FREECAD ASSEMBLY — COMPONENT RECIPES ("roommake")

This assembly document has 24 components, labeled P0..P23 below (a component is one placed body or linked part). 22 of them carry a construction recipe — the FreeCAD feature program that regenerates the part from scratch, quoted from this document or its linked companion documents; the rest are supplied as boundary geometry only. No exploded tour is included for this assembly.
NOTE — document 2 of 3 of this assembly tour. The two overview renders and the header above are repeated from document 1; the component sections below continue where the previous document stopped.
COMPONENT P14 — recipe-attached ("sofa", a linked part whose construction recipe lives in a companion FreeCAD document of the same project; that document's serialized recipe follows).
Construction recipe (the companion document, serialized — sketch geometry with constraints, then the solid features built on it; lengths are millimeters unless a unit is written):

FCSTD DOCUMENT  (FreeCAD 1.0R39109 (Git))
Label: sofa
License: All rights reserved
LicenseURL: https://en.wikipedia.org/wiki/All_rights_reserved
objects: Sketcher::SketchObject×17, PartDesign::Pad×14, PartDesign::Fillet×11, PartDesign::Plane×9, PartDesign::Body×9, PartDesign::ShapeBinder×8, PartDesign::Pocket×3, App::Part×3, Part::FeaturePython×2, PartDesign::LinearPattern×1
note: 148 computed .brp shape members not serialized (recipe doc carries the construction recipe); baked Part::Feature solids carry a one-line shape summary decoded from their .brp

FEATURE [Sketcher::SketchObject] Sketch
  ArcFitTolerance = 1e-06
  AttachmentSupport = -> [XZ_Plane]
  FullyConstrained = true
  MakeInternals = false
  MapMode = 5
  Placement = pos=(0,0,0) rot=(1,0,0;1.5708rad)
  sketch-geometry (4):
    g0: LineSegment StartX=-300 StartY=380 StartZ=0 EndX=-300 EndY=180 EndZ=0
    g1: LineSegment StartX=-300 StartY=180 StartZ=0 EndX=300 EndY=180 EndZ=0
    g2: LineSegment StartX=300 StartY=180 StartZ=0 EndX=300 EndY=380 EndZ=0
    g3: LineSegment StartX=300 StartY=380 StartZ=0 EndX=-300 EndY=380 EndZ=0
  constraints (11):
    c: Coincident(g0,g1)
    c: Coincident(g1,g2)
    c: Coincident(g2,g3)
    c: Coincident(g3,g0)
    c: Vertical(g0)
    c: Vertical(g2)
    c: Horizontal(g1)
    c: Distance(g0,g2) = 600
    c: Distance(g1,g3) = 200
    c: Symmetric(g0,g2,g-2)
    c: DistanceY(g-1,g1) = 180
FEATURE [PartDesign::Pad] Pad
  Direction = (0,-1,2e-16)
  Length = 700
  Length2 = 10
  Midplane = true
  Placement = pos=(0,0,0) rot=(1,0,0;1.5708rad)
  Profile = -> Sketch
  ReferenceAxis = -> Sketch [N_Axis]
  Refine = true
  Suppressed = false
  Type = 0
FEATURE [Sketcher::SketchObject] Sketch001
  ArcFitTolerance = 1e-06
  AttachmentSupport = -> [YZ_Plane]
  ExternalGeometry = -> [Pad]
  FullyConstrained = false
  MakeInternals = false
  MapMode = 5
  Placement = pos=(0,0,0) rot=(0.57735,0.57735,0.57735;2.0944rad)
  sketch-geometry (6):
    g0: LineSegment StartX=350 StartY=380 StartZ=0 EndX=420 EndY=599.2 EndZ=0
    g1: LineSegment [constr] StartX=350 StartY=380 StartZ=0 EndX=420 EndY=380 EndZ=0
    g2: LineSegment [constr] StartX=420 StartY=380 StartZ=0 EndX=420 EndY=599.2 EndZ=0
    g3: LineSegment StartX=420 StartY=599.2 StartZ=0 EndX=351.422 EndY=613.236 EndZ=0
    g4: LineSegment StartX=351.422 StartY=613.236 StartZ=0 EndX=280 EndY=380 EndZ=0
    g5: LineSegment StartX=280 StartY=380 StartZ=0 EndX=350 EndY=380 EndZ=0
  constraints (14):
    c: Coincident(g0,g-4)
    c: Coincident(g1,g0)
    c: Horizontal(g1)
    c: Coincident(g2,g1)
    c: Coincident(g2,g0)
    c: Vertical(g2)
    c: Coincident(g3,g0)
    c: PointOnObject(g4,g-3)
    c: Coincident(g5,g4)
    c: Coincident(g5,g0)
    c: DistanceX(g1,g1) = 70
    c: DistanceX(g5,g5) = 70
    c: Equal(g5,g3)
    c: Coincident(g4,g3)
FEATURE [PartDesign::Pad] Pad001
  BaseFeature = -> Pad
  Direction = (1,0,0)
  Length = 600
  Length2 = 10
  Midplane = true
  Placement = pos=(0,0,0) rot=(1,0,0;1.5708rad)
  Profile = -> Sketch001
  ReferenceAxis = -> Sketch001 [N_Axis]
  Suppressed = false
  Type = 0
FEATURE [Sketcher::SketchObject] Sketch002
  ArcFitTolerance = 1e-06
  AttachmentSupport = -> [Pad001]
  ExternalGeometry = -> [Pad001]
  FullyConstrained = false
  MakeInternals = false
  MapMode = 5
  Placement = pos=(300,0,0) rot=(0.707107,0,0.707107;3.14159rad)
  sketch-geometry (4):
    g0: LineSegment StartX=380 StartY=-280 StartZ=0 EndX=449.666 EndY=-80 EndZ=0
    g1: LineSegment StartX=449.666 StartY=-80 StartZ=0 EndX=880 EndY=-177.889 EndZ=0
    g2: LineSegment StartX=880 StartY=-177.889 StartZ=0 EndX=799.667 EndY=-408.511 EndZ=0
    g3: LineSegment StartX=799.667 StartY=-408.511 StartZ=0 EndX=380 EndY=-280 EndZ=0
  constraints (9):
    c: Coincident(g0,g-4)
    c: DistanceY(g0,g0) = 200
    c: Coincident(g1,g0)
    c: DistanceX(g0,g1) = 500
    c: Coincident(g2,g1)
    c: Coincident(g3,g2)
    c: Coincident(g3,g0)
    c: Parallel(g2,g0)
    c: Parallel(g3,g-3)
FEATURE [PartDesign::Pad] Pad002
  BaseFeature = -> Pad001
  Direction = (1,0,-2e-16)
  Length = 600
  Length2 = 10
  Placement = pos=(0,0,0) rot=(1,0,0;1.5708rad)
  Profile = -> Sketch002
  ReferenceAxis = -> Sketch002 [N_Axis]
  Reversed = true
  Suppressed = false
  Type = 0
FEATURE [Sketcher::SketchObject] Sketch003
  ArcFitTolerance = 1e-06
  AttachmentSupport = -> [Pad002]
  ExternalGeometry = -> [Pad002]
  FullyConstrained = false
  MakeInternals = false
  MapMode = 5
  Placement = pos=(300,0,0) rot=(0.707107,0,0.707107;3.14159rad)
  sketch-geometry (4):
    g0: LineSegment StartX=180 StartY=-350 StartZ=0 EndX=180 EndY=329.78 EndZ=0
    g1: LineSegment StartX=180 StartY=329.78 StartZ=0 EndX=100 EndY=329.78 EndZ=0
    g2: LineSegment StartX=100 StartY=329.78 StartZ=0 EndX=100 EndY=-350 EndZ=0
    g3: LineSegment StartX=100 StartY=-350 StartZ=0 EndX=180 EndY=-350 EndZ=0
  constraints (10):
    c: Coincident(g0,g1)
    c: Coincident(g1,g2)
    c: Coincident(g2,g3)
    c: Coincident(g3,g0)
    c: Vertical(g0)
    c: Vertical(g2)
    c: Horizontal(g1)
    c: Horizontal(g3)
    c: Coincident(g0,g-3)
    c: DistanceX(g1,g0) = 80
FEATURE [PartDesign::Pad] Pad003
  BaseFeature = -> Pad002
  Direction = (1,0,-2e-16)
  Length = 600
  Length2 = 10
  Placement = pos=(0,0,0) rot=(1,0,0;1.5708rad)
  Profile = -> Sketch003
  ReferenceAxis = -> Sketch003 [N_Axis]
  Refine = true
  Reversed = true
  Suppressed = false
  Type = 0
FEATURE [PartDesign::Fillet] Fillet
  Base = -> Pad003 [Edge9,Edge10]
  BaseFeature = -> Pad003
  Placement = pos=(0,0,0) rot=(1,0,0;1.5708rad)
  Radius = 10
  Refine = true
  SupportTransform = false
  Suppressed = false
  UseAllEdges = false
FEATURE [PartDesign::Fillet] Fillet001
  Base = -> Fillet [Edge4]
  BaseFeature = -> Fillet
  Placement = pos=(0,0,0) rot=(1,0,0;1.5708rad)
  Radius = 30
  Refine = true
  SupportTransform = false
  Suppressed = false
  UseAllEdges = false
FEATURE [PartDesign::Fillet] Fillet002
  Base = -> Fillet001 [Edge1]
  BaseFeature = -> Fillet001
  Placement = pos=(0,0,0) rot=(1,0,0;1.5708rad)
  Radius = 10
  Refine = true
  SupportTransform = false
  Suppressed = false
  UseAllEdges = false
FEATURE [PartDesign::Fillet] Fillet003
  Base = -> Fillet002 [Edge29,Edge41]
  BaseFeature = -> Fillet002
  Placement = pos=(0,0,0) rot=(1,0,0;1.5708rad)
  Radius = 10
  Refine = true
  SupportTransform = false
  Suppressed = false
  UseAllEdges = false
FEATURE [PartDesign::Fillet] Fillet004
  Base = -> Fillet003 [Edge52]
  BaseFeature = -> Fillet003
  Placement = pos=(0,0,0) rot=(1,0,0;1.5708rad)
  Radius = 30
  Refine = true
  SupportTransform = false
  Suppressed = false
  UseAllEdges = false
FEATURE [PartDesign::Fillet] Fillet005
  Base = -> Fillet004 [Edge27,Edge30,Edge36]
  BaseFeature = -> Fillet004
  Placement = pos=(0,0,0) rot=(1,0,0;1.5708rad)
  Radius = 80
  Refine = true
  SupportTransform = false
  Suppressed = false
  UseAllEdges = false
FEATURE [PartDesign::Fillet] Fillet006
  Base = -> Fillet005 [Edge8,Edge33]
  BaseFeature = -> Fillet005
  Placement = pos=(0,0,0) rot=(1,0,0;1.5708rad)
  Radius = 10
  Refine = true
  SupportTransform = false
  Suppressed = false
  UseAllEdges = false
FEATURE [PartDesign::Plane] DatumPlane
  AttachmentSupport = -> [Fillet006]
  Length = 60
  MapMode = 5
  Placement = pos=(300,0,0) rot=(0.707107,0,0.707107;3.14159rad)
  ResizeMode = 0
  Width = 60
FEATURE [PartDesign::LinearPattern] LinearPattern
  BaseFeature = -> Fillet006
  Direction = -> DatumPlane
  Length = 1200
  Mode = 0
  Occurrences = 3
  Offset = 600
  Originals = -> [Fillet006]
  Placement = pos=(0,0,0) rot=(1,0,0;1.5708rad)
  Refine = true
  Suppressed = false
  TransformMode = 1
FEATURE [Sketcher::SketchObject] Sketch004
  ArcFitTolerance = 1e-06
  AttachmentOffset = pos=(0,0,-80) rot=(0,0,1;0rad)
  AttachmentSupport = -> [LinearPattern]
  ExternalGeometry = -> [LinearPattern]
  FullyConstrained = false
  MakeInternals = false
  MapMode = 5
  Placement = pos=(0,-270,-1.78e-14) rot=(1,0,0;1.5708rad)
  sketch-geometry (8):
    g0: LineSegment StartX=-300 StartY=100 StartZ=0 EndX=-300 EndY=618.908 EndZ=0
    g1: LineSegment StartX=-300 StartY=618.908 StartZ=0 EndX=-450 EndY=618.908 EndZ=0
    g2: LineSegment StartX=-450 StartY=618.908 StartZ=0 EndX=-450 EndY=100 EndZ=0
    g3: LineSegment StartX=-450 StartY=100 StartZ=0 EndX=-300 EndY=100 EndZ=0
    g4: LineSegment StartX=1500 StartY=100 StartZ=0 EndX=1650 EndY=100 EndZ=0
    g5: LineSegment StartX=1650 StartY=100 StartZ=0 EndX=1650 EndY=618.908 EndZ=0
    g6: LineSegment StartX=1650 StartY=618.908 StartZ=0 EndX=1500 EndY=618.908 EndZ=0
    g7: LineSegment StartX=1500 StartY=618.908 StartZ=0 EndX=1500 EndY=100 EndZ=0
  constraints (21):
    c: Coincident(g0,g1)
    c: Coincident(g1,g2)
    c: Coincident(g2,g3)
    c: Coincident(g3,g0)
    c: Vertical(g0)
    c: Vertical(g2)
    c: Horizontal(g1)
    c: Horizontal(g3)
    c: Coincident(g0,g-4)
    c: Coincident(g4,g5)
    c: Coincident(g5,g6)
    c: Coincident(g6,g7)
    c: Coincident(g7,g4)
    c: Horizontal(g4)
    c: Horizontal(g6)
    c: Vertical(g5)
    c: Vertical(g7)
    c: Coincident(g4,g-4)
    c: Equal(g6,g1)
    c: DistanceX(g1,g1) = 150
    c: Equal(g2,g5)
FEATURE [PartDesign::Pad] Pad004
  BaseFeature = -> LinearPattern
  Direction = (0,-1,2e-16)
  Length = 620
  Length2 = 10
  Placement = pos=(0,0,0) rot=(1,0,0;1.5708rad)
  Profile = -> Sketch004
  ReferenceAxis = -> Sketch004 [N_Axis]
  Reversed = true
  Suppressed = false
  Type = 0
FEATURE [Sketcher::SketchObject] Sketch005
  ArcFitTolerance = 1e-06
  AttachmentSupport = -> [Pad004]
  ExternalGeometry = -> [Pad004]
  FullyConstrained = false
  MakeInternals = false
  MapMode = 5
  Placement = pos=(1650,0,0) rot=(0.707107,0,0.707107;3.14159rad)
  sketch-geometry (10):
    g0: Circle [constr] CenterX=618.908 CenterY=-350 CenterZ=0 NormalX=0 NormalY=0 NormalZ=1 AngleXU=0 Radius=1
    g1-g4: Circle [constr] x4 (B-spline internal-alignment scaffolding for g5; pole/knot coordinates omitted)
    g5: BSplineCurve PolesCount=4 KnotsCount=2 Degree=3 IsPeriodic=0
    g6: GeomPoint [constr] X=618.908 Y=-350 Z=0
    g7: GeomPoint [constr] X=544.087 Y=270 Z=0
    g8: LineSegment StartX=544.087 StartY=270 StartZ=0 EndX=618.908 EndY=270 EndZ=0
    g9: LineSegment StartX=618.908 StartY=-350 StartZ=0 EndX=618.908 EndY=270 EndZ=0
  constraints (15):
    c: Weight(g0) = 1
    c: Weight(g1) = 1
    c: Equal(g1,g2)
    c: Equal(g1,g3)
    c: Equal(g1,g4)
    c: InternalAlignment(g1-g4 -> g5) x4
    c: InternalAlignment(g6,g5)
    c: InternalAlignment(g7,g5)
    c: Coincident(g1,g0)
    c: PointOnObject(g4,g-4)
    c: Coincident(g-5,g5)
    c: Coincident(g9,g0)
    c: Coincident(g9,g8)
    c: Vertical(g9)
    c: Coincident(g5,g8)
FEATURE [PartDesign::Pocket] Pocket
  BaseFeature = -> Pad004
  Direction = (-1,0,2e-16)
  Length = 150
  Length2 = 5
  Placement = pos=(0,0,0) rot=(1,0,0;1.5708rad)
  Profile = -> Sketch005
  ReferenceAxis = -> Sketch005 [N_Axis]
  Suppressed = false
  Type = 0
FEATURE [Sketcher::SketchObject] Sketch006
  ArcFitTolerance = 1e-06
  AttachmentSupport = -> [Pocket]
  ExternalGeometry = -> [Pocket]
  FullyConstrained = false
  MakeInternals = false
  MapMode = 5
  Placement = pos=(-450,0,0) rot=(0.707107,0,-0.707107;3.14159rad)
  sketch-geometry (10):
    g0: Circle [constr] CenterX=-618.908 CenterY=-350 CenterZ=0 NormalX=0 NormalY=0 NormalZ=1 AngleXU=0 Radius=1
    g1-g4: Circle [constr] x4 (B-spline internal-alignment scaffolding for g5; pole/knot coordinates omitted)
    g5: BSplineCurve PolesCount=4 KnotsCount=2 Degree=3 IsPeriodic=0
    g6: GeomPoint [constr] X=-618.908 Y=-350 Z=0
    g7: GeomPoint [constr] X=-544.087 Y=270 Z=0
    g8: LineSegment StartX=-544.087 StartY=270 StartZ=0 EndX=-618.908 EndY=270 EndZ=0
    g9: LineSegment StartX=-618.908 StartY=-350 StartZ=0 EndX=-618.908 EndY=270 EndZ=0
  constraints (13):
    c: Weight(g0) = 1
    c: Weight(g1) = 1
    c: Equal(g1,g2)
    c: Equal(g1,g3)
    c: Equal(g1,g4)
    c: InternalAlignment(g1-g4 -> g5) x4
    c: InternalAlignment(g6,g5)
    c: InternalAlignment(g7,g5)
    c: Coincident(g1,g0)
    c: Coincident(g9,g0)
    c: Coincident(g9,g8)
    c: Vertical(g9)
    c: Coincident(g5,g8)
FEATURE [PartDesign::Pocket] Pocket001
  BaseFeature = -> Pocket
  Direction = (1,0,2e-16)
  Length = 150
  Length2 = 5
  Placement = pos=(0,0,0) rot=(1,0,0;1.5708rad)
  Profile = -> Sketch006
  ReferenceAxis = -> Sketch006 [N_Axis]
  Suppressed = false
  Type = 0
FEATURE [PartDesign::Fillet] Fillet007
  Base = -> Pocket001 [Edge94,Edge87]
  BaseFeature = -> Pocket001
  Placement = pos=(0,0,0) rot=(1,0,0;1.5708rad)
  Radius = 50
  SupportTransform = false
  Suppressed = false
  UseAllEdges = false
FEATURE [PartDesign::Fillet] Fillet008
  Base = -> Fillet007 [Edge18,Edge155]
  BaseFeature = -> Fillet007
  Placement = pos=(0,0,0) rot=(1,0,0;1.5708rad)
  Radius = 9.9
  Refine = true
  SupportTransform = false
  Suppressed = false
  UseAllEdges = false
FEATURE [PartDesign::Fillet] Fillet009
  Base = -> Fillet008 [Edge102,Edge54]
  BaseFeature = -> Fillet008
  Placement = pos=(0,0,0) rot=(1,0,0;1.5708rad)
  Radius = 100
  Refine = true
  SupportTransform = false
  Suppressed = false
  UseAllEdges = false
FEATURE [PartDesign::Fillet] Fillet010
  Base = -> Fillet009 [Edge147,Edge9]
  BaseFeature = -> Fillet009
  Placement = pos=(0,0,0) rot=(1,0,0;1.5708rad)
  Radius = 5
  Refine = true
  SupportTransform = false
  Suppressed = false
  UseAllEdges = false
FEATURE [Sketcher::SketchObject] Sketch007
  ArcFitTolerance = 1e-06
  AttachmentSupport = -> [Fillet010]
  ExternalGeometry = -> [Fillet010]
  FullyConstrained = false
  MakeInternals = false
  MapMode = 5
  Placement = pos=(0,3e-14,100) rot=(1,0,0;3.14159rad)
  sketch-geometry (14):
    g0: Circle CenterX=900 CenterY=235.906 CenterZ=0 NormalX=0 NormalY=0 NormalZ=1 AngleXU=0 Radius=25
    g1: Circle CenterX=300 CenterY=235.906 CenterZ=0 NormalX=0 NormalY=0 NormalZ=1 AngleXU=0 Radius=25
    g2: Circle CenterX=300 CenterY=-248.707 CenterZ=0 NormalX=0 NormalY=0 NormalZ=1 AngleXU=0 Radius=25
    g3: Circle CenterX=900 CenterY=-248.707 CenterZ=0 NormalX=0 NormalY=0 NormalZ=1 AngleXU=0 Radius=25
    g4: Circle CenterX=1408.78 CenterY=235.906 CenterZ=0 NormalX=0 NormalY=0 NormalZ=1 AngleXU=0 Radius=25
    g5: Circle CenterX=1408.78 CenterY=-248.707 CenterZ=0 NormalX=0 NormalY=0 NormalZ=1 AngleXU=0 Radius=25
    g6: Circle CenterX=-208.781 CenterY=-248.707 CenterZ=0 NormalX=0 NormalY=0 NormalZ=1 AngleXU=0 Radius=25
    g7: Circle CenterX=-208.781 CenterY=235.906 CenterZ=0 NormalX=0 NormalY=0 NormalZ=1 AngleXU=0 Radius=25
    g8: LineSegment [constr] StartX=900 StartY=320 StartZ=0 EndX=900 EndY=235.906 EndZ=0
    g9: LineSegment [constr] StartX=300 StartY=320 StartZ=0 EndX=300 EndY=235.906 EndZ=0
    g10: LineSegment [constr] StartX=900 StartY=235.906 StartZ=0 EndX=1408.78 EndY=235.906 EndZ=0
    g11: LineSegment [constr] StartX=300 StartY=235.906 StartZ=0 EndX=-208.781 EndY=235.906 EndZ=0
    g12: LineSegment [constr] StartX=-208.781 StartY=-248.707 StartZ=0 EndX=300 EndY=-248.707 EndZ=0
    g13: LineSegment [constr] StartX=1408.78 StartY=-248.707 StartZ=0 EndX=900 EndY=-248.707 EndZ=0
  constraints (33):
    c: Equal(g7,g1)
    c: Equal(g1,g0)
    c: Equal(g0,g4)
    c: Equal(g4,g5)
    c: Equal(g5,g3)
    c: Equal(g3,g2)
    c: Equal(g2,g6)
    c: Horizontal(g7,g1)
    c: Horizontal(g1,g0)
    c: Horizontal(g0,g4)
    c: Horizontal(g6,g2)
    c: Horizontal(g2,g3)
    c: Horizontal(g3,g5)
    c: Coincident(g8,g-4)
    c: Vertical(g8)
    c: Coincident(g9,g-3)
    c: Vertical(g9)
    c: Coincident(g10,g0)
    c: Coincident(g10,g4)
    c: Coincident(g11,g1)
    c: Coincident(g11,g7)
    c: Equal(g11,g10)
    c: Coincident(g12,g6)
    c: Coincident(g12,g2)
    c: Coincident(g13,g5)
    c: Coincident(g13,g3)
    c: Equal(g13,g12)
    c: Equal(g12,g10)
    c: Coincident(g1,g9)
    c: Coincident(g8,g0)
    c: Vertical(g0,g3)
    c: Vertical(g1,g2)
    c: Diameter(g7) = 50
FEATURE [PartDesign::Pad] Pad005
  BaseFeature = -> Fillet010
  Direction = (0,0,-1)
  Length = 100
  Length2 = 10
  Placement = pos=(0,0,0) rot=(1,0,0;1.5708rad)
  Profile = -> Sketch007
  ReferenceAxis = -> Sketch007 [N_Axis]
  Refine = true
  Suppressed = false
  TaperAngle = -5
  Type = 0
FEATURE [PartDesign::ShapeBinder] CopyPad005
  Placement = pos=(0,0,0) rot=(1,0,0;1.5708rad)
  TraceSupport = false
FEATURE [PartDesign::Plane] DatumPlane001
  AttachmentSupport = -> [CopyPad005]
  Length = 60
  MapMode = 5
  Placement = pos=(0,7.8e-15,100) rot=(1,0,0;3.14159rad)
  ResizeMode = 0
  Width = 60
FEATURE [Sketcher::SketchObject] Sketch008
  ArcFitTolerance = 1e-06
  AttachmentSupport = -> [DatumPlane001]
  ExternalGeometry = -> [CopyPad005]
  FullyConstrained = true
  MakeInternals = false
  MapMode = 5
  Placement = pos=(0,7.8e-15,100) rot=(1,0,0;3.14159rad)
  sketch-geometry (1):
    g0: Circle CenterX=-208.781 CenterY=235.906 CenterZ=0 NormalX=0 NormalY=0 NormalZ=1 AngleXU=0 Radius=25
  constraints (2):
    c: Coincident(g0,g-3)
    c: Equal(g0,g-3)
FEATURE [PartDesign::Pad] Pad006
  Direction = (0,0,-1)
  Length = 100
  Length2 = 10
  Placement = pos=(0,5.22e-14,100) rot=(1,0,0;3.14159rad)
  Profile = -> Sketch008
  ReferenceAxis = -> Sketch008 [N_Axis]
  Refine = true
  Suppressed = false
  TaperAngle = -5
  Type = 0
FEATURE [PartDesign::Body] Body001
  AllowCompound = false
  Group = -> [DatumPlane001,CopyPad005,Sketch008,Pad006]
  Origin = -> Origin003
  Placement = pos=(-600,0,0) rot=(0,0,1;0rad)
  Tip = -> Pad006
FEATURE [PartDesign::ShapeBinder] CopyPad006
  Placement = pos=(0,0,0) rot=(1,0,0;1.5708rad)
  TraceSupport = false
FEATURE [PartDesign::Plane] DatumPlane002
  AttachmentSupport = -> [CopyPad006]
  Length = 60
  MapMode = 5
  Placement = pos=(0,7.8e-15,100) rot=(1,0,0;3.14159rad)
  ResizeMode = 0
  Width = 60
FEATURE [Sketcher::SketchObject] Sketch009
  ArcFitTolerance = 1e-06
  AttachmentSupport = -> [DatumPlane002]
  ExternalGeometry = -> [CopyPad006]
  FullyConstrained = true
  MakeInternals = false
  MapMode = 5
  Placement = pos=(0,7.8e-15,100) rot=(1,0,0;3.14159rad)
  sketch-geometry (1):
    g0: Circle CenterX=300 CenterY=235.906 CenterZ=0 NormalX=0 NormalY=0 NormalZ=1 AngleXU=0 Radius=25
  constraints (2):
    c: Coincident(g0,g-3)
    c: Equal(g0,g-3)
FEATURE [PartDesign::Pad] Pad007
  Direction = (0,0,-1)
  Length = 100
  Length2 = 10
  Placement = pos=(0,7.44e-14,100) rot=(1,0,0;3.14159rad)
  Profile = -> Sketch009
  ReferenceAxis = -> Sketch009 [N_Axis]
  Refine = true
  Suppressed = false
  TaperAngle = -5
  Type = 0
FEATURE [PartDesign::Body] Body002
  AllowCompound = false
  Group = -> [DatumPlane002,CopyPad006,Sketch009,Pad007]
  Origin = -> Origin004
  Placement = pos=(-600,0,0) rot=(0,0,1;0rad)
  Tip = -> Pad007
FEATURE [PartDesign::ShapeBinder] CopyPad007
  Placement = pos=(0,0,0) rot=(1,0,0;1.5708rad)
  TraceSupport = false
FEATURE [PartDesign::Plane] DatumPlane003
  AttachmentSupport = -> [CopyPad007]
  Length = 60
  MapMode = 5
  Placement = pos=(0,7.8e-15,100) rot=(1,0,0;3.14159rad)
  ResizeMode = 0
  Width = 60
FEATURE [Sketcher::SketchObject] Sketch010
  ArcFitTolerance = 1e-06
  AttachmentSupport = -> [DatumPlane003]
  ExternalGeometry = -> [CopyPad007]
  FullyConstrained = true
  MakeInternals = false
  MapMode = 5
  Placement = pos=(0,7.8e-15,100) rot=(1,0,0;3.14159rad)
  sketch-geometry (1):
    g0: Circle CenterX=900 CenterY=235.906 CenterZ=0 NormalX=0 NormalY=0 NormalZ=1 AngleXU=0 Radius=25
  constraints (2):
    c: Coincident(g0,g-3)
    c: Equal(g0,g-3)
FEATURE [PartDesign::Pad] Pad008
  Direction = (0,0,-1)
  Length = 100
  Length2 = 10
  Placement = pos=(0,7.44e-14,100) rot=(1,0,0;3.14159rad)
  Profile = -> Sketch010
  ReferenceAxis = -> Sketch010 [N_Axis]
  Refine = true
  Suppressed = false
  TaperAngle = -5
  Type = 0
FEATURE [PartDesign::Body] Body003
  AllowCompound = false
  Group = -> [DatumPlane003,CopyPad007,Sketch010,Pad008]
  Origin = -> Origin006
  Placement = pos=(-600,0,0) rot=(0,0,1;0rad)
  Tip = -> Pad008
FEATURE [PartDesign::ShapeBinder] CopyPad008
  Placement = pos=(0,0,0) rot=(1,0,0;1.5708rad)
  TraceSupport = false
FEATURE [PartDesign::Plane] DatumPlane004
  AttachmentSupport = -> [CopyPad008]
  Length = 60
  MapMode = 5
  Placement = pos=(0,7.8e-15,100) rot=(1,0,0;3.14159rad)
  ResizeMode = 0
  Width = 60
FEATURE [Sketcher::SketchObject] Sketch011
  ArcFitTolerance = 1e-06
  AttachmentSupport = -> [DatumPlane004]
  ExternalGeometry = -> [CopyPad008]
  FullyConstrained = true
  MakeInternals = false
  MapMode = 5
  Placement = pos=(0,7.8e-15,100) rot=(1,0,0;3.14159rad)
  sketch-geometry (1):
    g0: Circle CenterX=1408.78 CenterY=235.906 CenterZ=0 NormalX=0 NormalY=0 NormalZ=1 AngleXU=0 Radius=25
  constraints (2):
    c: Coincident(g0,g-3)
    c: Equal(g0,g-3)
FEATURE [PartDesign::Pad] Pad009
  Direction = (0,0,-1)
  Length = 100
  Length2 = 10
  Placement = pos=(0,7.44e-14,100) rot=(1,0,0;3.14159rad)
  Profile = -> Sketch011
  ReferenceAxis = -> Sketch011 [N_Axis]
  Refine = true
  Suppressed = false
  TaperAngle = -5
  Type = 0
FEATURE [PartDesign::Body] Body004
  AllowCompound = false
  Group = -> [DatumPlane004,CopyPad008,Sketch011,Pad009]
  Origin = -> Origin007
  Placement = pos=(-600,0,0) rot=(0,0,1;0rad)
  Tip = -> Pad009
FEATURE [PartDesign::ShapeBinder] CopyPad009
  Placement = pos=(0,0,0) rot=(1,0,0;1.5708rad)
  TraceSupport = false
FEATURE [PartDesign::Plane] DatumPlane005
  AttachmentSupport = -> [CopyPad009]
  Length = 60
  MapMode = 5
  Placement = pos=(0,7.8e-15,100) rot=(1,0,0;3.14159rad)
  ResizeMode = 0
  Width = 60
FEATURE [Sketcher::SketchObject] Sketch012
  ArcFitTolerance = 1e-06
  AttachmentSupport = -> [DatumPlane005]
  ExternalGeometry = -> [CopyPad009]
  FullyConstrained = true
  MakeInternals = false
  MapMode = 5
  Placement = pos=(0,7.8e-15,100) rot=(1,0,0;3.14159rad)
  sketch-geometry (1):
    g0: Circle CenterX=-208.781 CenterY=-248.707 CenterZ=0 NormalX=0 NormalY=0 NormalZ=1 AngleXU=0 Radius=25
  constraints (2):
    c: Coincident(g0,g-3)
    c: Equal(g0,g-3)
FEATURE [PartDesign::Pad] Pad010
  Direction = (0,0,-1)
  Length = 100
  Length2 = 10
  Placement = pos=(0,7.44e-14,100) rot=(1,0,0;3.14159rad)
  Profile = -> Sketch012
  ReferenceAxis = -> Sketch012 [N_Axis]
  Refine = true
  Suppressed = false
  TaperAngle = -5
  Type = 0
FEATURE [PartDesign::Body] Body005
  AllowCompound = false
  Group = -> [DatumPlane005,CopyPad009,Sketch012,Pad010]
  Origin = -> Origin008
  Placement = pos=(-600,0,0) rot=(0,0,1;0rad)
  Tip = -> Pad010
FEATURE [PartDesign::ShapeBinder] CopyPad010
  Placement = pos=(0,0,0) rot=(1,0,0;1.5708rad)
  TraceSupport = false
FEATURE [PartDesign::Plane] DatumPlane006
  AttachmentSupport = -> [CopyPad010]
  Length = 60
  MapMode = 5
  Placement = pos=(0,7.8e-15,100) rot=(1,0,0;3.14159rad)
  ResizeMode = 0
  Width = 60
FEATURE [Sketcher::SketchObject] Sketch013
  ArcFitTolerance = 1e-06
  AttachmentSupport = -> [DatumPlane006]
  ExternalGeometry = -> [CopyPad010]
  FullyConstrained = true
  MakeInternals = false
  MapMode = 5
  Placement = pos=(0,7.8e-15,100) rot=(1,0,0;3.14159rad)
  sketch-geometry (1):
    g0: Circle CenterX=300 CenterY=-248.707 CenterZ=0 NormalX=0 NormalY=0 NormalZ=1 AngleXU=0 Radius=25
  constraints (2):
    c: Coincident(g0,g-3)
    c: Equal(g0,g-3)
FEATURE [PartDesign::Pad] Pad011
  Direction = (0,0,-1)
  Length = 100
  Length2 = 10
  Placement = pos=(0,7.44e-14,100) rot=(1,0,0;3.14159rad)
  Profile = -> Sketch013
  ReferenceAxis = -> Sketch013 [N_Axis]
  Refine = true
  Suppressed = false
  TaperAngle = -5
  Type = 0
FEATURE [PartDesign::Body] Body006
  AllowCompound = false
  Group = -> [DatumPlane006,CopyPad010,Sketch013,Pad011]
  Origin = -> Origin009
  Placement = pos=(-600,0,0) rot=(0,0,1;0rad)
  Tip = -> Pad011
FEATURE [PartDesign::ShapeBinder] CopyPad011
  Placement = pos=(0,0,0) rot=(1,0,0;1.5708rad)
  TraceSupport = false
FEATURE [PartDesign::Plane] DatumPlane007
  AttachmentSupport = -> [CopyPad011]
  Length = 60
  MapMode = 5
  Placement = pos=(0,7.8e-15,100) rot=(1,0,0;3.14159rad)
  ResizeMode = 0
  Width = 60
FEATURE [Sketcher::SketchObject] Sketch014
  ArcFitTolerance = 1e-06
  AttachmentSupport = -> [DatumPlane007]
  ExternalGeometry = -> [CopyPad011]
  FullyConstrained = true
  MakeInternals = false
  MapMode = 5
  Placement = pos=(0,7.8e-15,100) rot=(1,0,0;3.14159rad)
  sketch-geometry (1):
    g0: Circle CenterX=900 CenterY=-248.707 CenterZ=0 NormalX=0 NormalY=0 NormalZ=1 AngleXU=0 Radius=25
  constraints (2):
    c: Coincident(g0,g-3)
    c: Equal(g0,g-3)
FEATURE [PartDesign::Pad] Pad012
  Direction = (0,0,-1)
  Length = 100
  Length2 = 10
  Placement = pos=(0,3e-14,100) rot=(1,0,0;3.14159rad)
  Profile = -> Sketch014
  ReferenceAxis = -> Sketch014 [N_Axis]
  Refine = true
  Suppressed = false
  TaperAngle = -5
  Type = 0
FEATURE [PartDesign::Body] Body007
  AllowCompound = false
  Group = -> [DatumPlane007,CopyPad011,Sketch014,Pad012]
  Origin = -> Origin010
  Placement = pos=(-600,0,0) rot=(0,0,1;0rad)
  Tip = -> Pad012
FEATURE [PartDesign::ShapeBinder] CopyPad012
  Placement = pos=(0,0,0) rot=(1,0,0;1.5708rad)
  TraceSupport = false
FEATURE [PartDesign::Plane] DatumPlane008
  AttachmentSupport = -> [CopyPad012]
  Length = 60
  MapMode = 5
  Placement = pos=(0,7.8e-15,100) rot=(1,0,0;3.14159rad)
  ResizeMode = 0
  Width = 60
FEATURE [Sketcher::SketchObject] Sketch015
  ArcFitTolerance = 1e-06
  AttachmentSupport = -> [DatumPlane008]
  ExternalGeometry = -> [CopyPad012]
  FullyConstrained = true
  MakeInternals = false
  MapMode = 5
  Placement = pos=(0,7.8e-15,100) rot=(1,0,0;3.14159rad)
  sketch-geometry (1):
    g0: Circle CenterX=1408.78 CenterY=-248.707 CenterZ=0 NormalX=0 NormalY=0 NormalZ=1 AngleXU=0 Radius=25
  constraints (2):
    c: Coincident(g0,g-3)
    c: Equal(g0,g-3)
FEATURE [PartDesign::Pad] Pad013
  Direction = (0,0,-1)
  Length = 100
  Length2 = 10
  Placement = pos=(0,7.44e-14,100) rot=(1,0,0;3.14159rad)
  Profile = -> Sketch015
  ReferenceAxis = -> Sketch015 [N_Axis]
  Refine = true
  Suppressed = false
  TaperAngle = -5
  Type = 0
FEATURE [PartDesign::Body] Body008
  AllowCompound = false
  Group = -> [DatumPlane008,CopyPad012,Sketch015,Pad013]
  Origin = -> Origin011
  Placement = pos=(-600,0,0) rot=(0,0,1;0rad)
  Tip = -> Pad013
FEATURE [App::Part] Part  label="Foot"
  Group = -> [Body001,Body002,Body003,Body004,Body005,Body006,Body007,Body008]
  Origin = -> Origin005
  Placement = pos=(-600,0,0) rot=(0,0,1;0rad)
FEATURE [Part::FeaturePython] Clone001  label="foot_clone"  # Draft clone (typed FeaturePython)
  AttacherType = Attacher::AttachEngine3D
  Fuse = false
  Objects = -> [Part]
  Scale = (1,1,1)
FEATURE [Sketcher::SketchObject] Sketch016
  ArcFitTolerance = 1e-06
  AttachmentSupport = -> [Pad005]
  FullyConstrained = false
  MakeInternals = false
  MapMode = 5
  Placement = pos=(0,0,2.89e-14) rot=(1,0,0;3.14159rad)
  sketch-geometry (4):
    g0: LineSegment StartX=-340.164 StartY=321.267 StartZ=0 EndX=-340.164 EndY=-393.446 EndZ=0
    g1: LineSegment StartX=-340.164 StartY=-393.446 StartZ=0 EndX=1597.02 EndY=-393.446 EndZ=0
    g2: LineSegment StartX=1597.02 StartY=-393.446 StartZ=0 EndX=1597.02 EndY=321.267 EndZ=0
    g3: LineSegment StartX=1597.02 StartY=321.267 StartZ=0 EndX=-340.164 EndY=321.267 EndZ=0
  constraints (8):
    c: Coincident(g0,g1)
    c: Coincident(g1,g2)
    c: Coincident(g2,g3)
    c: Coincident(g3,g0)
    c: Vertical(g0)
    c: Vertical(g2)
    c: Horizontal(g1)
    c: Horizontal(g3)
FEATURE [PartDesign::Pocket] Pocket002
  BaseFeature = -> Pad005
  Direction = (0,0,1)
  Length = 100
  Length2 = 5
  Placement = pos=(0,0,0) rot=(1,0,0;1.5708rad)
  Profile = -> Sketch016
  ReferenceAxis = -> Sketch016 [N_Axis]
  Refine = true
  Suppressed = false
  Type = 0
FEATURE [PartDesign::Body] Body
  AllowCompound = false
  Group = -> [Sketch,Pad,Sketch001,Pad001,Sketch002,Pad002,Sketch003,Pad003,Fillet,Fillet001,Fillet002,Fillet003,Fillet004,Fillet005,Fillet006,DatumPlane,LinearPattern,Sketch004,Pad004,Sketch005,Pocket,Sketch006,Pocket001,Fillet007,Fillet008,Fillet009,Fillet010,Sketch007,Pad005,Sketch016,Pocket002]
  Origin = -> Origin
  Placement = pos=(-600,0,0) rot=(0,0,1;0rad)
  Tip = -> Pocket002
FEATURE [App::Part] Part001  label="body_p"
  Group = -> [Body]
  Origin = -> Origin012
  Placement = pos=(-600,0,0) rot=(0,0,1;0rad)
FEATURE [Part::FeaturePython] Clone  label="body_clone"  # Draft clone (typed FeaturePython)
  AttacherType = Attacher::AttachEngine3D
  Fuse = false
  Objects = -> [Part001]
  Scale = (1,1,1)
FEATURE [App::Part] Part002  label="sofa"
  Group = -> [Clone001,Clone]
  Origin = -> Origin013
COMPONENT P15 — recipe-attached ("table", a linked part whose construction recipe lives in a companion FreeCAD document of the same project; that document's serialized recipe follows).
Construction recipe (the companion document, serialized — sketch geometry with constraints, then the solid features built on it; lengths are millimeters unless a unit is written):

FCSTD DOCUMENT  (FreeCAD 1.0R39109 (Git))
Label: table
License: All rights reserved
LicenseURL: https://en.wikipedia.org/wiki/All_rights_reserved
objects: Sketcher::SketchObject×7, PartDesign::Pad×7, PartDesign::Pocket×2, App::Part×2, PartDesign::Body×1, Assembly::JointGroup×1, Part::FeaturePython×1
note: 43 computed .brp shape members not serialized (recipe doc carries the construction recipe); baked Part::Feature solids carry a one-line shape summary decoded from their .brp

FEATURE [Sketcher::SketchObject] Sketch
  ArcFitTolerance = 1e-06
  AttachmentSupport = -> [XY_Plane]
  FullyConstrained = true
  MakeInternals = false
  MapMode = 5
  sketch-geometry (5):
    g0: LineSegment StartX=-550 StartY=-350 StartZ=0 EndX=550 EndY=-350 EndZ=0
    g1: LineSegment StartX=550 StartY=-350 StartZ=0 EndX=550 EndY=350 EndZ=0
    g2: LineSegment StartX=550 StartY=350 StartZ=0 EndX=-550 EndY=350 EndZ=0
    g3: LineSegment StartX=-550 StartY=350 StartZ=0 EndX=-550 EndY=-350 EndZ=0
    g4: GeomPoint [constr] X=0 Y=0 Z=0
  constraints (12):
    c: Coincident(g0,g1)
    c: Coincident(g1,g2)
    c: Coincident(g2,g3)
    c: Coincident(g3,g0)
    c: Horizontal(g0)
    c: Horizontal(g2)
    c: Vertical(g1)
    c: Vertical(g3)
    c: Symmetric(g2,g0,g4)
    c: Coincident(g4,g-1)
    c: DistanceX(g2,g2) = 1100
    c: DistanceY(g3,g3) = 700
FEATURE [PartDesign::Pad] Pad
  Direction = (0,0,1)
  Length = 30
  Length2 = 10
  Profile = -> Sketch
  ReferenceAxis = -> Sketch [N_Axis]
  Refine = true
  Suppressed = false
  Type = 0
FEATURE [Sketcher::SketchObject] Sketch001
  ArcFitTolerance = 1e-06
  AttachmentSupport = -> [Pad]
  ExternalGeometry = -> [Pad]
  FullyConstrained = true
  MakeInternals = false
  MapMode = 5
  Placement = pos=(0,0,0) rot=(1,0,0;3.14159rad)
  sketch-geometry (16):
    g0: LineSegment StartX=-470 StartY=270 StartZ=0 EndX=-470 EndY=210 EndZ=0
    g1: LineSegment StartX=-470 StartY=210 StartZ=0 EndX=-410 EndY=210 EndZ=0
    g2: LineSegment StartX=-410 StartY=210 StartZ=0 EndX=-410 EndY=270 EndZ=0
    g3: LineSegment StartX=-410 StartY=270 StartZ=0 EndX=-470 EndY=270 EndZ=0
    g4: LineSegment StartX=410 StartY=270 StartZ=0 EndX=410 EndY=210 EndZ=0
    g5: LineSegment StartX=410 StartY=210 StartZ=0 EndX=470 EndY=210 EndZ=0
    g6: LineSegment StartX=470 StartY=210 StartZ=0 EndX=470 EndY=270 EndZ=0
    g7: LineSegment StartX=470 StartY=270 StartZ=0 EndX=410 EndY=270 EndZ=0
    g8: LineSegment StartX=410 StartY=-210 StartZ=0 EndX=410 EndY=-270 EndZ=0
    g9: LineSegment StartX=410 StartY=-270 StartZ=0 EndX=470 EndY=-270 EndZ=0
    g10: LineSegment StartX=470 StartY=-270 StartZ=0 EndX=470 EndY=-210 EndZ=0
    g11: LineSegment StartX=470 StartY=-210 StartZ=0 EndX=410 EndY=-210 EndZ=0
    g12: LineSegment StartX=-470 StartY=-210 StartZ=0 EndX=-470 EndY=-270 EndZ=0
    g13: LineSegment StartX=-470 StartY=-270 StartZ=0 EndX=-410 EndY=-270 EndZ=0
    g14: LineSegment StartX=-410 StartY=-270 StartZ=0 EndX=-410 EndY=-210 EndZ=0
    g15: LineSegment StartX=-410 StartY=-210 StartZ=0 EndX=-470 EndY=-210 EndZ=0
  constraints (48):
    c: Coincident(g0,g1)
    c: Coincident(g1,g2)
    c: Coincident(g2,g3)
    c: Coincident(g3,g0)
    c: Vertical(g0)
    c: Vertical(g2)
    c: Horizontal(g1)
    c: Horizontal(g3)
    c: DistanceX(g1,g1) = 60
    c: DistanceY(g2,g2) = 60
    c: DistanceX(g-4,g0) = 80
    c: DistanceY(g0,g-4) = 80
    c: Coincident(g4,g5)
    c: Coincident(g5,g6)
    c: Coincident(g6,g7)
    c: Coincident(g7,g4)
    c: Vertical(g4)
    c: Vertical(g6)
    c: Horizontal(g5)
    c: Horizontal(g7)
    c: Coincident(g8,g9)
    c: Coincident(g9,g10)
    c: Coincident(g10,g11)
    c: Coincident(g11,g8)
    c: Vertical(g8)
    c: Vertical(g10)
    c: Horizontal(g9)
    c: Horizontal(g11)
    c: Coincident(g12,g13)
    c: Coincident(g13,g14)
    c: Coincident(g14,g15)
    c: Coincident(g15,g12)
    c: Vertical(g12)
    c: Vertical(g14)
    c: Horizontal(g13)
    c: Horizontal(g15)
    c: Equal(g1,g15)
    c: Equal(g15,g11)
    c: Equal(g11,g7)
    c: Equal(g2,g6)
    c: Equal(g6,g10)
    c: Equal(g10,g14)
    c: DistanceX(g-6,g12) = 80
    c: DistanceX(g9,g-6) = 80
    c: DistanceX(g6,g-5) = 80
    c: DistanceY(g6,g-5) = 80
    c: DistanceY(g-6,g9) = 80
    c: DistanceY(g-6,g12) = 80
FEATURE [PartDesign::Pad] Pad001
  BaseFeature = -> Pad
  Direction = (0,0,-1)
  Length = 600
  Length2 = 10
  Profile = -> Sketch001
  ReferenceAxis = -> Sketch001 [N_Axis]
  Refine = true
  Suppressed = false
  Type = 0
FEATURE [Sketcher::SketchObject] Sketch002
  ArcFitTolerance = 1e-06
  AttachmentSupport = -> [Pad001]
  ExternalGeometry = -> [Pad001]
  FullyConstrained = true
  MakeInternals = false
  MapMode = 5
  Placement = pos=(0,-270,0) rot=(1,0,0;1.5708rad)
  sketch-geometry (12):
    g0: LineSegment StartX=470 StartY=-600 StartZ=0 EndX=470 EndY=-200 EndZ=0
    g1: LineSegment StartX=410 StartY=-600 StartZ=0 EndX=410 EndY=-200 EndZ=0
    g2: LineSegment StartX=410 StartY=-600 StartZ=0 EndX=417.5 EndY=-600 EndZ=0
    g3: LineSegment StartX=410 StartY=-200 StartZ=0 EndX=417.5 EndY=-600 EndZ=0
    g4: LineSegment StartX=470 StartY=-200 StartZ=0 EndX=462.5 EndY=-600 EndZ=0
    g5: LineSegment StartX=462.5 StartY=-600 StartZ=0 EndX=470 EndY=-600 EndZ=0
    g6: LineSegment StartX=-410 StartY=-600 StartZ=0 EndX=-410 EndY=-200 EndZ=0
    g7: LineSegment StartX=-470 StartY=-600 StartZ=0 EndX=-470 EndY=-200 EndZ=0
    g8: LineSegment StartX=-470 StartY=-200 StartZ=0 EndX=-462.5 EndY=-600 EndZ=0
    g9: LineSegment StartX=-417.5 StartY=-600 StartZ=0 EndX=-410 EndY=-200 EndZ=0
    g10: LineSegment StartX=-417.5 StartY=-600 StartZ=0 EndX=-410 EndY=-600 EndZ=0
    g11: LineSegment StartX=-462.5 StartY=-600 StartZ=0 EndX=-470 EndY=-600 EndZ=0
  constraints (33):
    c: Coincident(g0,g-3)
    c: Vertical(g0)
    c: DistanceY(g0,g0) = 400
    c: Coincident(g1,g-3)
    c: Vertical(g1)
    c: Equal(g1,g0)
    c: Coincident(g2,g1)
    c: Coincident(g5,g0)
    c: Coincident(g3,g1)
    c: Coincident(g4,g0)
    c: PointOnObject(g4,g5)
    c: Coincident(g2,g3)
    c: PointOnObject(g5,g4)
    c: DistanceX(g1,g2) = 7.5
    c: Equal(g5,g2)
    c: Coincident(g6,g-4)
    c: Vertical(g6)
    c: Coincident(g7,g-4)
    c: Vertical(g7)
    c: Equal(g6,g7)
    c: Equal(g7,g1)
    c: Coincident(g8,g7)
    c: PointOnObject(g8,g-4)
    c: PointOnObject(g9,g-4)
    c: Coincident(g9,g6)
    c: Coincident(g10,g9)
    c: Coincident(g10,g6)
    c: Coincident(g11,g8)
    c: Coincident(g11,g7)
    c: Equal(g10,g11)
    c: Equal(g11,g2)
    c: PointOnObject(g4,g-3)
    c: PointOnObject(g2,g-3)
FEATURE [PartDesign::Pocket] Pocket
  BaseFeature = -> Pad001
  Direction = (0,1,-2e-16)
  Length = 5
  Length2 = 5
  Profile = -> Sketch002
  ReferenceAxis = -> Sketch002 [N_Axis]
  Refine = true
  Suppressed = false
  Type = 1
FEATURE [Sketcher::SketchObject] Sketch003
  ArcFitTolerance = 1e-06
  AttachmentSupport = -> [Pocket]
  ExternalGeometry = -> [Pocket]
  FullyConstrained = true
  MakeInternals = false
  MapMode = 5
  Placement = pos=(-550,0,0) rot=(0.57735,-0.57735,-0.57735;2.0944rad)
  sketch-geometry (12):
    g0: LineSegment StartX=-270 StartY=-200 StartZ=0 EndX=-270 EndY=-600 EndZ=0
    g1: LineSegment StartX=-210 StartY=-200 StartZ=0 EndX=-210 EndY=-600 EndZ=0
    g2: LineSegment StartX=210 StartY=-200 StartZ=0 EndX=210 EndY=-600 EndZ=0
    g3: LineSegment StartX=270 StartY=-200 StartZ=0 EndX=270 EndY=-600 EndZ=0
    g4: LineSegment StartX=-270 StartY=-600 StartZ=0 EndX=-262.5 EndY=-600 EndZ=0
    g5: LineSegment StartX=210 StartY=-600 StartZ=0 EndX=217.5 EndY=-600 EndZ=0
    g6: LineSegment StartX=-270 StartY=-200 StartZ=0 EndX=-262.5 EndY=-600 EndZ=0
    g7: LineSegment StartX=-217.5 StartY=-600 StartZ=0 EndX=-210 EndY=-200 EndZ=0
    g8: LineSegment StartX=210 StartY=-200 StartZ=0 EndX=217.5 EndY=-600 EndZ=0
    g9: LineSegment StartX=262.5 StartY=-600 StartZ=0 EndX=270 EndY=-200 EndZ=0
    g10: LineSegment StartX=262.5 StartY=-600 StartZ=0 EndX=270 EndY=-600 EndZ=0
    g11: LineSegment StartX=-217.5 StartY=-600 StartZ=0 EndX=-210 EndY=-600 EndZ=0
  constraints (30):
    c: Coincident(g0,g-6)
    c: Coincident(g0,g-6)
    c: Coincident(g1,g-5)
    c: Coincident(g1,g-5)
    c: Coincident(g2,g-4)
    c: Coincident(g2,g-4)
    c: Coincident(g3,g-3)
    c: Coincident(g3,g-3)
    c: Coincident(g4,g0)
    c: Coincident(g11,g1)
    c: Coincident(g5,g2)
    c: Coincident(g10,g3)
    c: Coincident(g6,g0)
    c: PointOnObject(g7,g11)
    c: Coincident(g7,g1)
    c: Coincident(g8,g2)
    c: PointOnObject(g9,g10)
    c: Coincident(g9,g3)
    c: Coincident(g5,g8)
    c: PointOnObject(g10,g9)
    c: DistanceX(g10,g10) = 7.5
    c: Coincident(g4,g6)
    c: PointOnObject(g11,g7)
    c: Equal(g4,g11)
    c: Equal(g11,g5)
    c: Equal(g5,g10)
    c: Horizontal(g10)
    c: Horizontal(g5)
    c: Horizontal(g4)
    c: Horizontal(g11)
FEATURE [PartDesign::Pocket] Pocket001
  BaseFeature = -> Pocket
  Direction = (1,0,0)
  Length = 5
  Length2 = 5
  Profile = -> Sketch003
  ReferenceAxis = -> Sketch003 [N_Axis]
  Suppressed = false
  Type = 1
FEATURE [Sketcher::SketchObject] Sketch004
  ArcFitTolerance = 1e-06
  AttachmentSupport = -> [Pocket001]
  ExternalGeometry = -> [Pocket001]
  FullyConstrained = true
  MakeInternals = false
  MapMode = 5
  Placement = pos=(0,-270,0) rot=(1,0,0;1.5708rad)
  sketch-geometry (4):
    g0: LineSegment StartX=-410 StartY=0 StartZ=0 EndX=-410 EndY=-135 EndZ=0
    g1: LineSegment StartX=-410 StartY=-135 StartZ=0 EndX=410 EndY=-135 EndZ=0
    g2: LineSegment StartX=410 StartY=-135 StartZ=0 EndX=410 EndY=0 EndZ=0
    g3: LineSegment StartX=410 StartY=0 StartZ=0 EndX=-410 EndY=0 EndZ=0
  constraints (11):
    c: Coincident(g0,g1)
    c: Coincident(g1,g2)
    c: Coincident(g2,g3)
    c: Coincident(g3,g0)
    c: Vertical(g0)
    c: Vertical(g2)
    c: Horizontal(g1)
    c: Horizontal(g3)
    c: Coincident(g0,g-3)
    c: PointOnObject(g1,g-4)
    c: DistanceY(g2,g2) = 135
FEATURE [PartDesign::Pad] Pad002
  BaseFeature = -> Pocket001
  Direction = (0,-1,2e-16)
  Length = 10
  Length2 = 10
  Profile = -> Sketch004
  ReferenceAxis = -> Sketch004 [N_Axis]
  Suppressed = false
  Type = 3
  UpToFace = -> Pocket001 [Face21]
FEATURE [PartDesign::Pad] Pad003
  BaseFeature = -> Pad002
  Direction = (1,0,0)
  Length = 10
  Length2 = 10
  Profile = -> Pad002 [Face11]
  Suppressed = false
  Type = 3
  UpToFace = -> Pad002 [Face9]
FEATURE [PartDesign::Pad] Pad004
  BaseFeature = -> Pad003
  Direction = (-1,0,0)
  Length = 10
  Length2 = 10
  Profile = -> Pad003 [Face16]
  Suppressed = false
  Type = 3
  UpToFace = -> Pad003 [Face14]
FEATURE [Sketcher::SketchObject] Sketch005
  ArcFitTolerance = 1e-06
  AttachmentSupport = -> [Pad004]
  ExternalGeometry = -> [Pad004]
  FullyConstrained = true
  MakeInternals = false
  MapMode = 5
  Placement = pos=(0,-270,1.134e-13) rot=(1,0,0;1.5708rad)
  sketch-geometry (8):
    g0: LineSegment StartX=-250 StartY=-22.5 StartZ=0 EndX=-250 EndY=-112.5 EndZ=0
    g1: LineSegment StartX=-250 StartY=-112.5 StartZ=0 EndX=250 EndY=-112.5 EndZ=0
    g2: LineSegment StartX=250 StartY=-112.5 StartZ=0 EndX=250 EndY=-22.5 EndZ=0
    g3: LineSegment StartX=250 StartY=-22.5 StartZ=0 EndX=-250 EndY=-22.5 EndZ=0
    g4: LineSegment [constr] StartX=-250 StartY=-22.5 StartZ=0 EndX=250 EndY=-112.5 EndZ=0
    g5: LineSegment [constr] StartX=250 StartY=-22.5 StartZ=0 EndX=-2.84e-14 EndY=-67.5 EndZ=0
    g6: LineSegment [constr] StartX=-410 StartY=-1.137e-13 StartZ=0 EndX=410 EndY=-135 EndZ=0
    g7: LineSegment [constr] StartX=410 StartY=0 StartZ=0 EndX=0 EndY=-67.5 EndZ=0
  constraints (18):
    c: Coincident(g0,g1)
    c: Coincident(g1,g2)
    c: Coincident(g2,g3)
    c: Coincident(g3,g0)
    c: Vertical(g0)
    c: Horizontal(g1)
    c: DistanceY(g0,g0) = 90
    c: DistanceX(g3,g3) = 500
    c: Symmetric(g2,g0,g-2)
    c: Coincident(g4,g0)
    c: Coincident(g4,g1)
    c: Coincident(g5,g2)
    c: Symmetric(g4,g4,g5)
    c: Coincident(g6,g-6)
    c: Coincident(g6,g-5)
    c: Coincident(g7,g-5)
    c: Symmetric(g6,g6,g7)
    c: Coincident(g5,g7)
FEATURE [PartDesign::Pad] Pad005
  BaseFeature = -> Pad004
  Direction = (0,-1,2e-16)
  Length = 3
  Length2 = 10
  Profile = -> Sketch005
  ReferenceAxis = -> Sketch005 [N_Axis]
  Refine = true
  Suppressed = false
  Type = 0
FEATURE [Sketcher::SketchObject] Sketch006
  ArcFitTolerance = 1e-06
  AttachmentSupport = -> [Pad005]
  ExternalGeometry = -> [Pad005]
  FullyConstrained = true
  MakeInternals = false
  MapMode = 5
  Placement = pos=(0,-273,0) rot=(1,0,0;1.5708rad)
  sketch-geometry (8):
    g0: LineSegment StartX=-55 StartY=-57.5 StartZ=0 EndX=-55 EndY=-77.5 EndZ=0
    g1: LineSegment StartX=-55 StartY=-77.5 StartZ=0 EndX=55 EndY=-77.5 EndZ=0
    g2: LineSegment StartX=55 StartY=-77.5 StartZ=0 EndX=55 EndY=-57.5 EndZ=0
    g3: LineSegment StartX=55 StartY=-57.5 StartZ=0 EndX=-55 EndY=-57.5 EndZ=0
    g4: LineSegment [constr] StartX=-55 StartY=-57.5 StartZ=0 EndX=55 EndY=-77.5 EndZ=0
    g5: LineSegment [constr] StartX=55 StartY=-57.5 StartZ=0 EndX=-2.84e-14 EndY=-67.5 EndZ=0
    g6: LineSegment [constr] StartX=-250 StartY=-22.5 StartZ=0 EndX=250 EndY=-112.5 EndZ=0
    g7: LineSegment [constr] StartX=250 StartY=-22.5 StartZ=0 EndX=-2.84e-14 EndY=-67.5 EndZ=0
  constraints (18):
    c: Coincident(g0,g1)
    c: Coincident(g1,g2)
    c: Coincident(g2,g3)
    c: Coincident(g3,g0)
    c: Vertical(g0)
    c: Horizontal(g1)
    c: DistanceX(g3,g3) = 110
    c: DistanceY(g2,g2) = 20
    c: Coincident(g4,g0)
    c: Coincident(g4,g1)
    c: Coincident(g5,g2)
    c: Symmetric(g2,g0,g-2)
    c: Symmetric(g0,g1,g5)
    c: Coincident(g6,g-4)
    c: Coincident(g6,g-3)
    c: Coincident(g7,g-3)
    c: Symmetric(g6,g6,g7)
    c: Coincident(g5,g7)
FEATURE [PartDesign::Pad] Pad006
  BaseFeature = -> Pad005
  Direction = (0,-1,2e-16)
  Length = 10
  Length2 = 10
  Profile = -> Sketch006
  ReferenceAxis = -> Sketch006 [N_Axis]
  Refine = true
  Suppressed = false
  Type = 0
FEATURE [PartDesign::Body] Body  label="table_b"
  AllowCompound = false
  Group = -> [Sketch,Pad,Sketch001,Pad001,Sketch002,Pocket,Sketch003,Pocket001,Sketch004,Pad002,Pad003,Pad004,Sketch005,Pad005,Sketch006,Pad006]
  Origin = -> Origin
  Placement = pos=(0,0,600) rot=(0,0,1;0rad)
  Tip = -> Pad006
FEATURE [Assembly::JointGroup] Joints
FEATURE [App::Part] Part  label="table_p"
  Group = -> [Body]
  Origin = -> Origin001
  Placement = pos=(0,0,600) rot=(0,0,1;0rad)
FEATURE [Part::FeaturePython] Clone  label="table_clone"  # Draft clone (typed FeaturePython)
  AttacherType = Attacher::AttachEngine3D
  Fuse = false
  Objects = -> [Part]
  Scale = (1,1,1)
FEATURE [App::Part] Part001  label="table"
  Group = -> [Clone]
  Origin = -> Origin002
COMPONENT P16 — same part as P15; its construction recipe is shown at P15.
COMPONENT P17 — recipe-attached ("table02", a linked part whose construction recipe lives in a companion FreeCAD document of the same project; that document's serialized recipe follows).
Construction recipe (the companion document, serialized — sketch geometry with constraints, then the solid features built on it; lengths are millimeters unless a unit is written):

FCSTD DOCUMENT  (FreeCAD 1.0R39109 (Git))
Label: table02
License: All rights reserved
LicenseURL: https://en.wikipedia.org/wiki/All_rights_reserved
objects: Sketcher::SketchObject×8, PartDesign::Pad×6, PartDesign::Body×6, Part::FeaturePython×6, PartDesign::Pocket×2, App::Part×1
note: 52 computed .brp shape members not serialized (recipe doc carries the construction recipe); baked Part::Feature solids carry a one-line shape summary decoded from their .brp

FEATURE [Sketcher::SketchObject] Sketch
  ArcFitTolerance = 1e-06
  AttachmentSupport = -> [XY_Plane]
  FullyConstrained = false
  MakeInternals = false
  MapMode = 5
  sketch-geometry (24):
    g0: LineSegment [constr] StartX=-600 StartY=-225 StartZ=0 EndX=600 EndY=-225 EndZ=0
    g1: LineSegment [constr] StartX=600 StartY=-225 StartZ=0 EndX=600 EndY=225 EndZ=0
    g2: LineSegment [constr] StartX=600 StartY=225 StartZ=0 EndX=-600 EndY=225 EndZ=0
    g3: LineSegment [constr] StartX=-600 StartY=225 StartZ=0 EndX=-600 EndY=-225 EndZ=0
    g4: GeomPoint [constr] X=0 Y=0 Z=0
    g5: LineSegment [constr] StartX=-600 StartY=225 StartZ=0 EndX=-600 EndY=265 EndZ=0
    g6: LineSegment [constr] StartX=-600 StartY=265 StartZ=0 EndX=-560 EndY=265 EndZ=0
    g7: LineSegment [constr] StartX=-560 StartY=265 StartZ=0 EndX=-560 EndY=185 EndZ=0
    g8: Circle CenterX=-560 CenterY=185 CenterZ=0 NormalX=0 NormalY=0 NormalZ=1 AngleXU=0 Radius=20
    g9: LineSegment [constr] StartX=-600 StartY=-225 StartZ=0 EndX=-600 EndY=-265 EndZ=0
    g10: LineSegment [constr] StartX=-600 StartY=-265 StartZ=0 EndX=-560 EndY=-265 EndZ=0
    g11: LineSegment [constr] StartX=-560 StartY=-265 StartZ=0 EndX=-560 EndY=-185 EndZ=0
    g12: Circle CenterX=-560 CenterY=-185 CenterZ=0 NormalX=0 NormalY=0 NormalZ=1 AngleXU=0 Radius=20
    g13: Circle CenterX=560 CenterY=185 CenterZ=0 NormalX=0 NormalY=0 NormalZ=1 AngleXU=0 Radius=20
    g14: Circle CenterX=560 CenterY=-185.063 CenterZ=0 NormalX=0 NormalY=0 NormalZ=1 AngleXU=0 Radius=20
    g15: LineSegment [constr] StartX=-560 StartY=185 StartZ=0 EndX=-560 EndY=175 EndZ=0
    g16: LineSegment [constr] StartX=-560 StartY=175 StartZ=0 EndX=-570 EndY=175 EndZ=0
    g17: LineSegment [constr] StartX=-570 StartY=175 StartZ=0 EndX=-570 EndY=195 EndZ=0
    g18: LineSegment [constr] StartX=560 StartY=-185.063 StartZ=0 EndX=570 EndY=-185.063 EndZ=0
    g19: LineSegment [constr] StartX=570 StartY=-185.063 StartZ=0 EndX=570 EndY=-195.063 EndZ=0
    g20: LineSegment [constr] StartX=-570 StartY=195 StartZ=0 EndX=-570 EndY=-195.063 EndZ=0
    g21: LineSegment [constr] StartX=-570 StartY=-195.063 StartZ=0 EndX=570 EndY=-195.063 EndZ=0
    g22: LineSegment [constr] StartX=570 StartY=-195.063 StartZ=0 EndX=570 EndY=195 EndZ=0
    g23: LineSegment [constr] StartX=570 StartY=195 StartZ=0 EndX=-570 EndY=195 EndZ=0
  constraints (61):
    c: Coincident(g0,g1)
    c: Coincident(g1,g2)
    c: Coincident(g2,g3)
    c: Coincident(g3,g0)
    c: Horizontal(g0)
    c: Horizontal(g2)
    c: Vertical(g1)
    c: Vertical(g3)
    c: Symmetric(g2,g0,g4)
    c: Distance(g1,g3) = 1200
    c: Distance(g0,g2) = 450
    c: Coincident(g4,g-1)
    c: Coincident(g5,g2)
    c: Vertical(g5)
    c: DistanceY(g5,g5) = 40
    c: Distance(g6) = 40
    c: Coincident(g6,g5)
    c: Horizontal(g6)
    c: Distance(g7) = 80
    c: Coincident(g7,g6)
    c: Vertical(g7)
    c: Diameter(g8) = 40
    c: Coincident(g8,g7)
    c: Distance(g9) = 40
    c: Coincident(g9,g0)
    c: Vertical(g9)
    c: Distance(g10) = 40
    c: Coincident(g10,g9)
    c: Horizontal(g10)
    c: Distance(g11) = 80
    c: Coincident(g11,g10)
    c: Vertical(g11)
    c: Diameter(g12) = 40
    c: Coincident(g12,g11)
    c: Diameter(g13) = 40
    c: Diameter(g14) = 40
    c: Distance(g15) = 10
    c: Coincident(g15,g7)
    c: Vertical(g15)
    c: Distance(g16) = 10
    c: Coincident(g16,g15)
    c: Horizontal(g16)
    c: Distance(g17) = 20
    c: Coincident(g17,g16)
    c: Vertical(g17)
    c: Distance(g18) = 10
    c: Coincident(g18,g14)
    c: Horizontal(g18)
    c: Distance(g19) = 10
    c: Coincident(g19,g18)
    c: Vertical(g19)
    c: Coincident(g20,g21)
    c: Coincident(g21,g22)
    c: Coincident(g22,g23)
    c: Coincident(g23,g20)
    c: Vertical(g20)
    c: Vertical(g22)
    c: Horizontal(g21)
    c: Horizontal(g23)
    c: Coincident(g20,g17)
    c: Coincident(g21,g19)
FEATURE [PartDesign::Pad] Pad
  Direction = (0,0,1)
  Length = 780
  Length2 = 10
  Profile = -> Sketch
  ReferenceAxis = -> Sketch [N_Axis]
  Refine = true
  Suppressed = false
  Type = 0
FEATURE [PartDesign::Body] Body
  AllowCompound = false
  Group = -> [Sketch,Pad]
  Origin = -> Origin
  Tip = -> Pad
FEATURE [Sketcher::SketchObject] Sketch001
  ArcFitTolerance = 1e-06
  AttachmentSupport = -> [XY_Plane001]
  FullyConstrained = false
  MakeInternals = false
  MapMode = 5
  sketch-geometry (21):
    g0: LineSegment [constr] StartX=-600 StartY=-225 StartZ=0 EndX=600 EndY=-225 EndZ=0
    g1: LineSegment [constr] StartX=600 StartY=-225 StartZ=0 EndX=600 EndY=225 EndZ=0
    g2: LineSegment [constr] StartX=600 StartY=225 StartZ=0 EndX=-600 EndY=225 EndZ=0
    g3: LineSegment [constr] StartX=-600 StartY=225 StartZ=0 EndX=-600 EndY=-225 EndZ=0
    g4: GeomPoint [constr] X=0 Y=0 Z=0
    g5: LineSegment [constr] StartX=-600 StartY=225 StartZ=0 EndX=-600 EndY=265 EndZ=0
    g6: LineSegment [constr] StartX=-600 StartY=265 StartZ=0 EndX=-560 EndY=265 EndZ=0
    g7: LineSegment [constr] StartX=-560 StartY=265 StartZ=0 EndX=-560 EndY=185 EndZ=0
    g8: Circle CenterX=-560 CenterY=185 CenterZ=0 NormalX=0 NormalY=0 NormalZ=1 AngleXU=0 Radius=20
    g9: LineSegment [constr] StartX=-600 StartY=-225 StartZ=0 EndX=-600 EndY=-265 EndZ=0
    g10: LineSegment [constr] StartX=-600 StartY=-265 StartZ=0 EndX=-560 EndY=-265 EndZ=0
    g11: LineSegment [constr] StartX=-560 StartY=-265 StartZ=0 EndX=-560 EndY=-185 EndZ=0
    g12: Circle CenterX=-560 CenterY=-185 CenterZ=0 NormalX=0 NormalY=0 NormalZ=1 AngleXU=0 Radius=20
    g13: Circle CenterX=560 CenterY=185 CenterZ=0 NormalX=0 NormalY=0 NormalZ=1 AngleXU=0 Radius=20
    g14: LineSegment [constr] StartX=-560 StartY=185 StartZ=0 EndX=-560 EndY=175 EndZ=0
    g15: LineSegment [constr] StartX=-560 StartY=175 StartZ=0 EndX=-570 EndY=175 EndZ=0
    g16: LineSegment [constr] StartX=-570 StartY=175 StartZ=0 EndX=-570 EndY=195 EndZ=0
    g17: LineSegment [constr] StartX=-570 StartY=195 StartZ=0 EndX=-570 EndY=-195.063 EndZ=0
    g18: LineSegment [constr] StartX=-570 StartY=-195.063 StartZ=0 EndX=570 EndY=-195.063 EndZ=0
    g19: LineSegment [constr] StartX=570 StartY=-195.063 StartZ=0 EndX=570 EndY=195 EndZ=0
    g20: LineSegment [constr] StartX=570 StartY=195 StartZ=0 EndX=-570 EndY=195 EndZ=0
  constraints (52):
    c: Coincident(g0,g1)
    c: Coincident(g1,g2)
    c: Coincident(g2,g3)
    c: Coincident(g3,g0)
    c: Horizontal(g0)
    c: Horizontal(g2)
    c: Vertical(g1)
    c: Vertical(g3)
    c: Symmetric(g2,g0,g4)
    c: Distance(g1,g3) = 1200
    c: Distance(g0,g2) = 450
    c: Coincident(g4,g-1)
    c: Coincident(g5,g2)
    c: Vertical(g5)
    c: DistanceY(g5,g5) = 40
    c: Distance(g6) = 40
    c: Coincident(g6,g5)
    c: Horizontal(g6)
    c: Distance(g7) = 80
    c: Coincident(g7,g6)
    c: Vertical(g7)
    c: Diameter(g8) = 40
    c: Coincident(g8,g7)
    c: Distance(g9) = 40
    c: Coincident(g9,g0)
    c: Vertical(g9)
    c: Distance(g10) = 40
    c: Coincident(g10,g9)
    c: Horizontal(g10)
    c: Distance(g11) = 80
    c: Coincident(g11,g10)
    c: Vertical(g11)
    c: Diameter(g12) = 40
    c: Coincident(g12,g11)
    c: Diameter(g13) = 40
    c: Distance(g14) = 10
    c: Coincident(g14,g7)
    c: Vertical(g14)
    c: Distance(g15) = 10
    c: Coincident(g15,g14)
    c: Horizontal(g15)
    c: Distance(g16) = 20
    c: Coincident(g16,g15)
    c: Vertical(g16)
    c: Coincident(g17,g18)
    c: Coincident(g19,g20)
    c: Coincident(g20,g17)
    c: Vertical(g17)
    c: Vertical(g19)
    c: Horizontal(g18)
    c: Horizontal(g20)
    c: Coincident(g17,g16)
FEATURE [PartDesign::Pad] Pad001
  Direction = (0,0,1)
  Length = 780
  Length2 = 10
  Profile = -> Sketch001
  ReferenceAxis = -> Sketch001 [N_Axis]
  Refine = true
  Suppressed = false
  Type = 0
FEATURE [PartDesign::Body] Body001
  AllowCompound = false
  Group = -> [Sketch001,Pad001]
  Origin = -> Origin001
  Tip = -> Pad001
FEATURE [Sketcher::SketchObject] Sketch002
  ArcFitTolerance = 1e-06
  AttachmentSupport = -> [XY_Plane002]
  FullyConstrained = false
  MakeInternals = false
  MapMode = 5
  sketch-geometry (22):
    g0: LineSegment [constr] StartX=-600 StartY=-225 StartZ=0 EndX=600 EndY=-225 EndZ=0
    g1: LineSegment [constr] StartX=600 StartY=-225 StartZ=0 EndX=600 EndY=225 EndZ=0
    g2: LineSegment [constr] StartX=600 StartY=225 StartZ=0 EndX=-600 EndY=225 EndZ=0
    g3: LineSegment [constr] StartX=-600 StartY=225 StartZ=0 EndX=-600 EndY=-225 EndZ=0
    g4: GeomPoint [constr] X=0 Y=0 Z=0
    g5: LineSegment [constr] StartX=-600 StartY=225 StartZ=0 EndX=-600 EndY=265 EndZ=0
    g6: LineSegment [constr] StartX=-600 StartY=265 StartZ=0 EndX=-560 EndY=265 EndZ=0
    g7: LineSegment [constr] StartX=-560 StartY=265 StartZ=0 EndX=-560 EndY=185 EndZ=0
    g8: Circle CenterX=-560 CenterY=185 CenterZ=0 NormalX=0 NormalY=0 NormalZ=1 AngleXU=0 Radius=20
    g9: LineSegment [constr] StartX=-600 StartY=-225 StartZ=0 EndX=-600 EndY=-265 EndZ=0
    g10: LineSegment [constr] StartX=-600 StartY=-265 StartZ=0 EndX=-560 EndY=-265 EndZ=0
    g11: LineSegment [constr] StartX=-560 StartY=-265 StartZ=0 EndX=-560 EndY=-185 EndZ=0
    g12: Circle CenterX=-560 CenterY=-185 CenterZ=0 NormalX=0 NormalY=0 NormalZ=1 AngleXU=0 Radius=20
    g13: LineSegment [constr] StartX=-560 StartY=185 StartZ=0 EndX=-560 EndY=175 EndZ=0
    g14: LineSegment [constr] StartX=-560 StartY=175 StartZ=0 EndX=-570 EndY=175 EndZ=0
    g15: LineSegment [constr] StartX=-570 StartY=175 StartZ=0 EndX=-570 EndY=195 EndZ=0
    g16: LineSegment [constr] StartX=560 StartY=-185.063 StartZ=0 EndX=570 EndY=-185.063 EndZ=0
    g17: LineSegment [constr] StartX=570 StartY=-185.063 StartZ=0 EndX=570 EndY=-195.063 EndZ=0
    g18: LineSegment [constr] StartX=-570 StartY=195 StartZ=0 EndX=-570 EndY=-195.063 EndZ=0
    g19: LineSegment [constr] StartX=-570 StartY=-195.063 StartZ=0 EndX=570 EndY=-195.063 EndZ=0
    g20: LineSegment [constr] StartX=570 StartY=-195.063 StartZ=0 EndX=570 EndY=195 EndZ=0
    g21: LineSegment [constr] StartX=570 StartY=195 StartZ=0 EndX=-570 EndY=195 EndZ=0
  constraints (58):
    c: Coincident(g0,g1)
    c: Coincident(g1,g2)
    c: Coincident(g2,g3)
    c: Coincident(g3,g0)
    c: Horizontal(g0)
    c: Horizontal(g2)
    c: Vertical(g1)
    c: Vertical(g3)
    c: Symmetric(g2,g0,g4)
    c: Distance(g1,g3) = 1200
    c: Distance(g0,g2) = 450
    c: Coincident(g4,g-1)
    c: Coincident(g5,g2)
    c: Vertical(g5)
    c: DistanceY(g5,g5) = 40
    c: Distance(g6) = 40
    c: Coincident(g6,g5)
    c: Horizontal(g6)
    c: Distance(g7) = 80
    c: Coincident(g7,g6)
    c: Vertical(g7)
    c: Diameter(g8) = 40
    c: Coincident(g8,g7)
    c: Distance(g9) = 40
    c: Coincident(g9,g0)
    c: Vertical(g9)
    c: Distance(g10) = 40
    c: Coincident(g10,g9)
    c: Horizontal(g10)
    c: Distance(g11) = 80
    c: Coincident(g11,g10)
    c: Vertical(g11)
    c: Diameter(g12) = 40
    c: Coincident(g12,g11)
    c: Distance(g13) = 10
    c: Coincident(g13,g7)
    c: Vertical(g13)
    c: Distance(g14) = 10
    c: Coincident(g14,g13)
    c: Horizontal(g14)
    c: Distance(g15) = 20
    c: Coincident(g15,g14)
    c: Vertical(g15)
    c: Distance(g16) = 10
    c: Horizontal(g16)
    c: Distance(g17) = 10
    c: Coincident(g17,g16)
    c: Vertical(g17)
    c: Coincident(g18,g19)
    c: Coincident(g19,g20)
    c: Coincident(g20,g21)
    c: Coincident(g21,g18)
    c: Vertical(g18)
    c: Vertical(g20)
    c: Horizontal(g19)
    c: Horizontal(g21)
    c: Coincident(g18,g15)
    c: Coincident(g19,g17)
FEATURE [PartDesign::Pad] Pad002
  Direction = (0,0,1)
  Length = 780
  Length2 = 10
  Profile = -> Sketch002
  ReferenceAxis = -> Sketch002 [N_Axis]
  Refine = true
  Suppressed = false
  Type = 0
FEATURE [PartDesign::Body] Body002
  AllowCompound = false
  Group = -> [Sketch002,Pad002]
  Origin = -> Origin002
  Tip = -> Pad002
FEATURE [Sketcher::SketchObject] Sketch003
  ArcFitTolerance = 1e-06
  AttachmentSupport = -> [XY_Plane003]
  FullyConstrained = false
  MakeInternals = false
  MapMode = 5
  sketch-geometry (21):
    g0: LineSegment [constr] StartX=-600 StartY=-225 StartZ=0 EndX=600 EndY=-225 EndZ=0
    g1: LineSegment [constr] StartX=600 StartY=-225 StartZ=0 EndX=600 EndY=225 EndZ=0
    g2: LineSegment [constr] StartX=600 StartY=225 StartZ=0 EndX=-600 EndY=225 EndZ=0
    g3: LineSegment [constr] StartX=-600 StartY=225 StartZ=0 EndX=-600 EndY=-225 EndZ=0
    g4: GeomPoint [constr] X=0 Y=0 Z=0
    g5: LineSegment [constr] StartX=-600 StartY=225 StartZ=0 EndX=-600 EndY=265 EndZ=0
    g6: LineSegment [constr] StartX=-600 StartY=265 StartZ=0 EndX=-560 EndY=265 EndZ=0
    g7: LineSegment [constr] StartX=-560 StartY=265 StartZ=0 EndX=-560 EndY=185 EndZ=0
    g8: Circle CenterX=-560 CenterY=185 CenterZ=0 NormalX=0 NormalY=0 NormalZ=1 AngleXU=0 Radius=20
    g9: LineSegment [constr] StartX=-600 StartY=-225 StartZ=0 EndX=-600 EndY=-265 EndZ=0
    g10: LineSegment [constr] StartX=-600 StartY=-265 StartZ=0 EndX=-560 EndY=-265 EndZ=0
    g11: LineSegment [constr] StartX=-560 StartY=-265 StartZ=0 EndX=-560 EndY=-185 EndZ=0
    g12: LineSegment [constr] StartX=-560 StartY=185 StartZ=0 EndX=-560 EndY=175 EndZ=0
    g13: LineSegment [constr] StartX=-560 StartY=175 StartZ=0 EndX=-570 EndY=175 EndZ=0
    g14: LineSegment [constr] StartX=-570 StartY=175 StartZ=0 EndX=-570 EndY=195 EndZ=0
    g15: LineSegment [constr] StartX=560 StartY=-185.063 StartZ=0 EndX=570 EndY=-185.063 EndZ=0
    g16: LineSegment [constr] StartX=570 StartY=-185.063 StartZ=0 EndX=570 EndY=-195.063 EndZ=0
    g17: LineSegment [constr] StartX=-570 StartY=195 StartZ=0 EndX=-570 EndY=-195.063 EndZ=0
    g18: LineSegment [constr] StartX=-570 StartY=-195.063 StartZ=0 EndX=570 EndY=-195.063 EndZ=0
    g19: LineSegment [constr] StartX=570 StartY=-195.063 StartZ=0 EndX=570 EndY=195 EndZ=0
    g20: LineSegment [constr] StartX=570 StartY=195 StartZ=0 EndX=-570 EndY=195 EndZ=0
  constraints (56):
    c: Coincident(g0,g1)
    c: Coincident(g1,g2)
    c: Coincident(g2,g3)
    c: Coincident(g3,g0)
    c: Horizontal(g0)
    c: Horizontal(g2)
    c: Vertical(g1)
    c: Vertical(g3)
    c: Symmetric(g2,g0,g4)
    c: Distance(g1,g3) = 1200
    c: Distance(g0,g2) = 450
    c: Coincident(g4,g-1)
    c: Coincident(g5,g2)
    c: Vertical(g5)
    c: DistanceY(g5,g5) = 40
    c: Distance(g6) = 40
    c: Coincident(g6,g5)
    c: Horizontal(g6)
    c: Distance(g7) = 80
    c: Coincident(g7,g6)
    c: Vertical(g7)
    c: Diameter(g8) = 40
    c: Coincident(g8,g7)
    c: Distance(g9) = 40
    c: Coincident(g9,g0)
    c: Vertical(g9)
    c: Distance(g10) = 40
    c: Coincident(g10,g9)
    c: Horizontal(g10)
    c: Distance(g11) = 80
    c: Coincident(g11,g10)
    c: Vertical(g11)
    c: Distance(g12) = 10
    c: Coincident(g12,g7)
    c: Vertical(g12)
    c: Distance(g13) = 10
    c: Coincident(g13,g12)
    c: Horizontal(g13)
    c: Distance(g14) = 20
    c: Coincident(g14,g13)
    c: Vertical(g14)
    c: Distance(g15) = 10
    c: Horizontal(g15)
    c: Distance(g16) = 10
    c: Coincident(g16,g15)
    c: Vertical(g16)
    c: Coincident(g17,g18)
    c: Coincident(g18,g19)
    c: Coincident(g19,g20)
    c: Coincident(g20,g17)
    c: Vertical(g17)
    c: Vertical(g19)
    c: Horizontal(g18)
    c: Horizontal(g20)
    c: Coincident(g17,g14)
    c: Coincident(g18,g16)
FEATURE [PartDesign::Pad] Pad003
  Direction = (0,0,1)
  Length = 780
  Length2 = 10
  Profile = -> Sketch003
  ReferenceAxis = -> Sketch003 [N_Axis]
  Refine = true
  Suppressed = false
  Type = 0
FEATURE [PartDesign::Body] Body003
  AllowCompound = false
  Group = -> [Sketch003,Pad003]
  Origin = -> Origin003
  Tip = -> Pad003
FEATURE [Sketcher::SketchObject] Sketch004
  ArcFitTolerance = 1e-06
  AttachmentSupport = -> [XY_Plane004]
  FullyConstrained = false
  MakeInternals = false
  MapMode = 5
  sketch-geometry (20):
    g0: LineSegment [constr] StartX=-600 StartY=-225 StartZ=0 EndX=600 EndY=-225 EndZ=0
    g1: LineSegment [constr] StartX=600 StartY=-225 StartZ=0 EndX=600 EndY=225 EndZ=0
    g2: LineSegment [constr] StartX=600 StartY=225 StartZ=0 EndX=-600 EndY=225 EndZ=0
    g3: LineSegment [constr] StartX=-600 StartY=225 StartZ=0 EndX=-600 EndY=-225 EndZ=0
    g4: GeomPoint [constr] X=0 Y=0 Z=0
    g5: LineSegment [constr] StartX=-600 StartY=225 StartZ=0 EndX=-600 EndY=265 EndZ=0
    g6: LineSegment [constr] StartX=-600 StartY=265 StartZ=0 EndX=-560 EndY=265 EndZ=0
    g7: LineSegment [constr] StartX=-560 StartY=265 StartZ=0 EndX=-560 EndY=185 EndZ=0
    g8: LineSegment [constr] StartX=-600 StartY=-225 StartZ=0 EndX=-600 EndY=-265 EndZ=0
    g9: LineSegment [constr] StartX=-600 StartY=-265 StartZ=0 EndX=-560 EndY=-265 EndZ=0
    g10: LineSegment [constr] StartX=-560 StartY=-265 StartZ=0 EndX=-560 EndY=-185 EndZ=0
    g11: LineSegment [constr] StartX=-560 StartY=185 StartZ=0 EndX=-560 EndY=175 EndZ=0
    g12: LineSegment [constr] StartX=-560 StartY=175 StartZ=0 EndX=-570 EndY=175 EndZ=0
    g13: LineSegment [constr] StartX=-570 StartY=175 StartZ=0 EndX=-570 EndY=195 EndZ=0
    g14: LineSegment [constr] StartX=560 StartY=-185.063 StartZ=0 EndX=570 EndY=-185.063 EndZ=0
    g15: LineSegment [constr] StartX=570 StartY=-185.063 StartZ=0 EndX=570 EndY=-195.063 EndZ=0
    g16: LineSegment StartX=-570 StartY=195 StartZ=0 EndX=-570 EndY=-195.063 EndZ=0
    g17: LineSegment StartX=-570 StartY=-195.063 StartZ=0 EndX=570 EndY=-195.063 EndZ=0
    g18: LineSegment StartX=570 StartY=-195.063 StartZ=0 EndX=570 EndY=195 EndZ=0
    g19: LineSegment StartX=570 StartY=195 StartZ=0 EndX=-570 EndY=195 EndZ=0
  constraints (54):
    c: Coincident(g0,g1)
    c: Coincident(g1,g2)
    c: Coincident(g2,g3)
    c: Coincident(g3,g0)
    c: Horizontal(g0)
    c: Horizontal(g2)
    c: Vertical(g1)
    c: Vertical(g3)
    c: Symmetric(g2,g0,g4)
    c: Distance(g1,g3) = 1200
    c: Distance(g0,g2) = 450
    c: Coincident(g4,g-1)
    c: Coincident(g5,g2)
    c: Vertical(g5)
    c: DistanceY(g5,g5) = 40
    c: Distance(g6) = 40
    c: Coincident(g6,g5)
    c: Horizontal(g6)
    c: Distance(g7) = 80
    c: Coincident(g7,g6)
    c: Vertical(g7)
    c: Distance(g8) = 40
    c: Coincident(g8,g0)
    c: Vertical(g8)
    c: Distance(g9) = 40
    c: Coincident(g9,g8)
    c: Horizontal(g9)
    c: Distance(g10) = 80
    c: Coincident(g10,g9)
    c: Vertical(g10)
    c: Distance(g11) = 10
    c: Coincident(g11,g7)
    c: Vertical(g11)
    c: Distance(g12) = 10
    c: Coincident(g12,g11)
    c: Horizontal(g12)
    c: Distance(g13) = 20
    c: Coincident(g13,g12)
    c: Vertical(g13)
    c: Distance(g14) = 10
    c: Horizontal(g14)
    c: Distance(g15) = 10
    c: Coincident(g15,g14)
    c: Vertical(g15)
    c: Coincident(g16,g17)
    c: Coincident(g17,g18)
    c: Coincident(g18,g19)
    c: Coincident(g19,g16)
    c: Vertical(g16)
    c: Vertical(g18)
    c: Horizontal(g17)
    c: Horizontal(g19)
    c: Coincident(g16,g13)
    c: Coincident(g17,g15)
FEATURE [PartDesign::Pad] Pad004
  Direction = (0,0,1)
  Length = 220
  Length2 = 10
  Profile = -> Sketch004
  ReferenceAxis = -> Sketch004 [N_Axis]
  Refine = true
  Suppressed = false
  Type = 0
FEATURE [Sketcher::SketchObject] Sketch005
  ArcFitTolerance = 1e-06
  AttachmentSupport = -> [Pad004]
  ExternalGeometry = -> [Pad004]
  FullyConstrained = true
  MakeInternals = false
  MapMode = 5
  Placement = pos=(0,0,0) rot=(1,0,0;3.14159rad)
  sketch-geometry (4):
    g0: LineSegment StartX=-570 StartY=195.063 StartZ=0 EndX=-570 EndY=-195 EndZ=0
    g1: LineSegment StartX=-570 StartY=-195 StartZ=0 EndX=570 EndY=-195 EndZ=0
    g2: LineSegment StartX=570 StartY=-195 StartZ=0 EndX=570 EndY=195.063 EndZ=0
    g3: LineSegment StartX=570 StartY=195.063 StartZ=0 EndX=-570 EndY=195.063 EndZ=0
  constraints (10):
    c: Coincident(g0,g1)
    c: Coincident(g1,g2)
    c: Coincident(g2,g3)
    c: Coincident(g3,g0)
    c: Vertical(g0)
    c: Vertical(g2)
    c: Horizontal(g1)
    c: Horizontal(g3)
    c: Coincident(g0,g-3)
    c: Coincident(g1,g-4)
FEATURE [PartDesign::Pocket] Pocket
  BaseFeature = -> Pad004
  Direction = (0,0,1)
  Length = 180
  Length2 = 5
  Profile = -> Sketch005
  ReferenceAxis = -> Sketch005 [N_Axis]
  Refine = true
  Suppressed = false
  Type = 0
FEATURE [PartDesign::Body] Body004
  AllowCompound = false
  Group = -> [Sketch004,Pad004,Sketch005,Pocket]
  Origin = -> Origin004
  Tip = -> Pocket
FEATURE [Sketcher::SketchObject] Sketch006
  ArcFitTolerance = 1e-06
  AttachmentSupport = -> [XY_Plane005]
  FullyConstrained = false
  MakeInternals = false
  MapMode = 5
  sketch-geometry (16):
    g0: LineSegment StartX=-600 StartY=-225 StartZ=0 EndX=600 EndY=-225 EndZ=0
    g1: LineSegment StartX=600 StartY=-225 StartZ=0 EndX=600 EndY=225 EndZ=0
    g2: LineSegment StartX=600 StartY=225 StartZ=0 EndX=-600 EndY=225 EndZ=0
    g3: LineSegment StartX=-600 StartY=225 StartZ=0 EndX=-600 EndY=-225 EndZ=0
    g4: GeomPoint [constr] X=0 Y=0 Z=0
    g5: LineSegment [constr] StartX=-600 StartY=225 StartZ=0 EndX=-600 EndY=265 EndZ=0
    g6: LineSegment [constr] StartX=-600 StartY=265 StartZ=0 EndX=-560 EndY=265 EndZ=0
    g7: LineSegment [constr] StartX=-560 StartY=265 StartZ=0 EndX=-560 EndY=185 EndZ=0
    g8: LineSegment [constr] StartX=-600 StartY=-225 StartZ=0 EndX=-600 EndY=-265 EndZ=0
    g9: LineSegment [constr] StartX=-600 StartY=-265 StartZ=0 EndX=-560 EndY=-265 EndZ=0
    g10: LineSegment [constr] StartX=-560 StartY=-265 StartZ=0 EndX=-560 EndY=-185 EndZ=0
    g11: LineSegment [constr] StartX=-560 StartY=185 StartZ=0 EndX=-560 EndY=175 EndZ=0
    g12: LineSegment [constr] StartX=-560 StartY=175 StartZ=0 EndX=-570 EndY=175 EndZ=0
    g13: LineSegment [constr] StartX=-570 StartY=175 StartZ=0 EndX=-570 EndY=195 EndZ=0
    g14: LineSegment [constr] StartX=560 StartY=-185.063 StartZ=0 EndX=570 EndY=-185.063 EndZ=0
    g15: LineSegment [constr] StartX=570 StartY=-185.063 StartZ=0 EndX=570 EndY=-195.063 EndZ=0
  constraints (44):
    c: Coincident(g0,g1)
    c: Coincident(g1,g2)
    c: Coincident(g2,g3)
    c: Coincident(g3,g0)
    c: Horizontal(g0)
    c: Horizontal(g2)
    c: Vertical(g1)
    c: Vertical(g3)
    c: Symmetric(g2,g0,g4)
    c: Distance(g1,g3) = 1200
    c: Distance(g0,g2) = 450
    c: Coincident(g4,g-1)
    c: Coincident(g5,g2)
    c: Vertical(g5)
    c: DistanceY(g5,g5) = 40
    c: Distance(g6) = 40
    c: Coincident(g6,g5)
    c: Horizontal(g6)
    c: Distance(g7) = 80
    c: Coincident(g7,g6)
    c: Vertical(g7)
    c: Distance(g8) = 40
    c: Coincident(g8,g0)
    c: Vertical(g8)
    c: Distance(g9) = 40
    c: Coincident(g9,g8)
    c: Horizontal(g9)
    c: Distance(g10) = 80
    c: Coincident(g10,g9)
    c: Vertical(g10)
    c: Distance(g11) = 10
    c: Coincident(g11,g7)
    c: Vertical(g11)
    c: Distance(g12) = 10
    c: Coincident(g12,g11)
    c: Horizontal(g12)
    c: Distance(g13) = 20
    c: Coincident(g13,g12)
    c: Vertical(g13)
    c: Distance(g14) = 10
    c: Horizontal(g14)
    c: Distance(g15) = 10
    c: Coincident(g15,g14)
    c: Vertical(g15)
FEATURE [PartDesign::Pad] Pad005
  Direction = (0,0,1)
  Length = 800
  Length2 = 10
  Profile = -> Sketch006
  ReferenceAxis = -> Sketch006 [N_Axis]
  Refine = true
  Suppressed = false
  Type = 0
FEATURE [Sketcher::SketchObject] Sketch007
  ArcFitTolerance = 1e-06
  AttachmentSupport = -> [Pad005]
  ExternalGeometry = -> [Pad005]
  FullyConstrained = true
  MakeInternals = false
  MapMode = 5
  Placement = pos=(0,0,0) rot=(1,0,0;3.14159rad)
  sketch-geometry (4):
    g0: LineSegment StartX=-600 StartY=225 StartZ=0 EndX=-600 EndY=-225 EndZ=0
    g1: LineSegment StartX=-600 StartY=-225 StartZ=0 EndX=600 EndY=-225 EndZ=0
    g2: LineSegment StartX=600 StartY=-225 StartZ=0 EndX=600 EndY=225 EndZ=0
    g3: LineSegment StartX=600 StartY=225 StartZ=0 EndX=-600 EndY=225 EndZ=0
  constraints (10):
    c: Coincident(g0,g1)
    c: Coincident(g1,g2)
    c: Coincident(g2,g3)
    c: Coincident(g3,g0)
    c: Vertical(g0)
    c: Vertical(g2)
    c: Horizontal(g1)
    c: Horizontal(g3)
    c: Coincident(g0,g-3)
    c: Coincident(g1,g-4)
FEATURE [PartDesign::Pocket] Pocket001
  BaseFeature = -> Pad005
  Direction = (0,0,1)
  Length = 760
  Length2 = 5
  Profile = -> Sketch007
  ReferenceAxis = -> Sketch007 [N_Axis]
  Refine = true
  Suppressed = false
  Type = 0
FEATURE [PartDesign::Body] Body005
  AllowCompound = false
  Group = -> [Sketch006,Pad005,Sketch007,Pocket001]
  Origin = -> Origin005
  Tip = -> Pocket001
FEATURE [Part::FeaturePython] Clone  label="foot1_clone"  # Draft clone (typed FeaturePython)
  AttacherType = Attacher::AttachEngine3D
  Fuse = false
  Objects = -> [Body]
  Scale = (1,1,1)
FEATURE [Part::FeaturePython] Clone001  label="foot2_clone"  # Draft clone (typed FeaturePython)
  AttacherType = Attacher::AttachEngine3D
  Fuse = false
  Objects = -> [Body001]
  Scale = (1,1,1)
FEATURE [Part::FeaturePython] Clone002  label="foot3_clone"  # Draft clone (typed FeaturePython)
  AttacherType = Attacher::AttachEngine3D
  Fuse = false
  Objects = -> [Body002]
  Scale = (1,1,1)
FEATURE [Part::FeaturePython] Clone003  label="foot4_clone"  # Draft clone (typed FeaturePython)
  AttacherType = Attacher::AttachEngine3D
  Fuse = false
  Objects = -> [Body003]
  Scale = (1,1,1)
FEATURE [Part::FeaturePython] Clone004  label="plate1_clone"  # Draft clone (typed FeaturePython)
  AttacherType = Attacher::AttachEngine3D
  Fuse = false
  Objects = -> [Body004]
  Scale = (1,1,1)
FEATURE [Part::FeaturePython] Clone005  label="plate2_clone"  # Draft clone (typed FeaturePython)
  AttacherType = Attacher::AttachEngine3D
  Fuse = false
  Objects = -> [Body005]
  Scale = (1,1,1)
FEATURE [App::Part] Part  label="table02"
  Group = -> [Clone,Clone001,Clone002,Clone003,Clone004,Clone005]
  Origin = -> Origin006
COMPONENT P18 — recipe-attached ("toasteroven", a linked part whose construction recipe lives in a companion FreeCAD document of the same project; that document's serialized recipe follows).
Construction recipe (the companion document, serialized — sketch geometry with constraints, then the solid features built on it; lengths are millimeters unless a unit is written):

FCSTD DOCUMENT  (FreeCAD 1.0R39109 (Git))
Label: toasteroven
License: All rights reserved
LicenseURL: https://en.wikipedia.org/wiki/All_rights_reserved
objects: Sketcher::SketchObject×24, PartDesign::Pad×14, PartDesign::Fillet×14, PartDesign::ShapeBinder×13, PartDesign::Pocket×10, PartDesign::Line×8, PartDesign::Body×6, Part::FeaturePython×6, PartDesign::Plane×2, App::Part×1
note: 197 computed .brp shape members not serialized (recipe doc carries the construction recipe); baked Part::Feature solids carry a one-line shape summary decoded from their .brp

FEATURE [Sketcher::SketchObject] Sketch
  ArcFitTolerance = 1e-06
  AttachmentSupport = -> [XY_Plane]
  FullyConstrained = true
  MakeInternals = false
  MapMode = 5
  sketch-geometry (5):
    g0: LineSegment StartX=-250 StartY=-230 StartZ=0 EndX=250 EndY=-230 EndZ=0
    g1: LineSegment StartX=250 StartY=-230 StartZ=0 EndX=250 EndY=230 EndZ=0
    g2: LineSegment StartX=250 StartY=230 StartZ=0 EndX=-250 EndY=230 EndZ=0
    g3: LineSegment StartX=-250 StartY=230 StartZ=0 EndX=-250 EndY=-230 EndZ=0
    g4: GeomPoint [constr] X=0 Y=0 Z=0
  constraints (12):
    c: Coincident(g0,g1)
    c: Coincident(g1,g2)
    c: Coincident(g2,g3)
    c: Coincident(g3,g0)
    c: Horizontal(g0)
    c: Horizontal(g2)
    c: Vertical(g1)
    c: Vertical(g3)
    c: Symmetric(g2,g0,g4)
    c: Distance(g1,g3) = 500
    c: Distance(g0,g2) = 460
    c: Coincident(g4,g-1)
FEATURE [PartDesign::Pad] Pad
  Direction = (0,0,1)
  Length = 14
  Length2 = 10
  Profile = -> Sketch
  ReferenceAxis = -> Sketch [N_Axis]
  Refine = true
  Suppressed = false
  Type = 0
FEATURE [Sketcher::SketchObject] Sketch001
  ArcFitTolerance = 1e-06
  AttachmentSupport = -> [Pad]
  FullyConstrained = true
  MakeInternals = false
  MapMode = 5
  Placement = pos=(0,0,14) rot=(0,0,1;0rad)
  sketch-geometry (5):
    g0: LineSegment StartX=-254.5 StartY=-234 StartZ=0 EndX=254.5 EndY=-234 EndZ=0
    g1: LineSegment StartX=254.5 StartY=-234 StartZ=0 EndX=254.5 EndY=234 EndZ=0
    g2: LineSegment StartX=254.5 StartY=234 StartZ=0 EndX=-254.5 EndY=234 EndZ=0
    g3: LineSegment StartX=-254.5 StartY=234 StartZ=0 EndX=-254.5 EndY=-234 EndZ=0
    g4: GeomPoint [constr] X=0 Y=0 Z=0
  constraints (12):
    c: Coincident(g0,g1)
    c: Coincident(g1,g2)
    c: Coincident(g2,g3)
    c: Coincident(g3,g0)
    c: Horizontal(g0)
    c: Horizontal(g2)
    c: Vertical(g1)
    c: Vertical(g3)
    c: Symmetric(g2,g0,g4)
    c: Distance(g1,g3) = 509
    c: Distance(g0,g2) = 468
    c: Coincident(g4,g-1)
FEATURE [PartDesign::Pad] Pad001
  BaseFeature = -> Pad
  Direction = (0,0,1)
  Length = 400
  Length2 = 10
  Profile = -> Sketch001
  ReferenceAxis = -> Sketch001 [N_Axis]
  Refine = true
  Suppressed = false
  Type = 0
FEATURE [Sketcher::SketchObject] Sketch002
  ArcFitTolerance = 1e-06
  AttachmentSupport = -> [Pad001]
  ExternalGeometry = -> [Pad001]
  FullyConstrained = false
  MakeInternals = false
  MapMode = 5
  Placement = pos=(0,-234,0) rot=(1,0,0;1.5708rad)
  sketch-geometry (23):
    g0: LineSegment StartX=-254.5 StartY=414 StartZ=0 EndX=-254.5 EndY=124 EndZ=0
    g1: LineSegment StartX=-254.5 StartY=124 StartZ=0 EndX=254.5 EndY=124 EndZ=0
    g2: LineSegment StartX=254.5 StartY=124 StartZ=0 EndX=254.5 EndY=414 EndZ=0
    g3: LineSegment StartX=254.5 StartY=414 StartZ=0 EndX=-254.5 EndY=414 EndZ=0
    g4: LineSegment [constr] StartX=-254.5 StartY=124 StartZ=0 EndX=-254.5 EndY=119 EndZ=0
    g5: LineSegment StartX=-254.5 StartY=119 StartZ=0 EndX=-254.5 EndY=14 EndZ=0
    g6: LineSegment StartX=-254.5 StartY=14 StartZ=0 EndX=254.5 EndY=14 EndZ=0
    g7: LineSegment StartX=254.5 StartY=14 StartZ=0 EndX=254.5 EndY=119 EndZ=0
    g8: LineSegment StartX=254.5 StartY=119 StartZ=0 EndX=-254.5 EndY=119 EndZ=0
    g9: LineSegment StartX=-175 StartY=317.961 StartZ=0 EndX=-175 EndY=220.039 EndZ=0
    g10: LineSegment StartX=-160 StartY=205.039 StartZ=0 EndX=160 EndY=205.039 EndZ=0
    g11: LineSegment StartX=175 StartY=220.039 StartZ=0 EndX=175 EndY=317.961 EndZ=0
    g12: LineSegment StartX=160 StartY=332.961 StartZ=0 EndX=-160 EndY=332.961 EndZ=0
    g13: LineSegment [constr] StartX=0 StartY=414 StartZ=0 EndX=8.1e-15 EndY=124 EndZ=0
    g14: LineSegment [constr] StartX=-175 StartY=332.961 StartZ=0 EndX=0 EndY=269 EndZ=0
    g15: ArcOfCircle CenterX=-160 CenterY=317.961 CenterZ=0 NormalX=0 NormalY=0 NormalZ=1 AngleXU=0 Radius=15 StartAngle=1.5708 EndAngle=3.14159
    g16: GeomPoint [constr] X=-175 Y=332.961 Z=0
    g17: ArcOfCircle CenterX=-160 CenterY=220.039 CenterZ=0 NormalX=0 NormalY=0 NormalZ=1 AngleXU=0 Radius=15 StartAngle=3.14159 EndAngle=4.71239
    g18: GeomPoint [constr] X=-175 Y=205.039 Z=0
    g19: ArcOfCircle CenterX=160 CenterY=220.039 CenterZ=0 NormalX=0 NormalY=0 NormalZ=1 AngleXU=0 Radius=15 StartAngle=4.71239 EndAngle=6.28319
    g20: GeomPoint [constr] X=175 Y=205.039 Z=0
    g21: ArcOfCircle CenterX=160 CenterY=317.961 CenterZ=0 NormalX=0 NormalY=0 NormalZ=1 AngleXU=0 Radius=15 StartAngle=-1.7195e-12 EndAngle=1.5708
    g22: GeomPoint [constr] X=175 Y=332.961 Z=0
  constraints (54):
    c: Coincident(g0,g1)
    c: Coincident(g1,g2)
    c: Coincident(g2,g3)
    c: Coincident(g3,g0)
    c: Vertical(g0)
    c: Vertical(g2)
    c: Horizontal(g1)
    c: Horizontal(g3)
    c: Distance(g1,g3) = 290
    c: Coincident(g0,g-3)
    c: PointOnObject(g1,g-4)
    c: Coincident(g4,g0)
    c: PointOnObject(g4,g-3)
    c: DistanceY(g4,g4) = 5
    c: Coincident(g5,g6)
    c: Coincident(g6,g7)
    c: Coincident(g7,g8)
    c: Coincident(g8,g5)
    c: Vertical(g5)
    c: Vertical(g7)
    c: Horizontal(g6)
    c: Horizontal(g8)
    c: Coincident(g5,g4)
    c: Coincident(g6,g-4)
    c: Vertical(g9)
    c: Vertical(g11)
    c: Horizontal(g10)
    c: DistanceX(g16,g22) = 350
    c: Symmetric(g16,g22,g-2)
    c: PointOnObject(g13,g-2)
    c: Symmetric(g1,g1,g13)
    c: PointOnObject(g13,g3)
    c: Coincident(g14,g16)
    c: Symmetric(g13,g13,g14)
    c: PointOnObject(g16,g12)
    c: PointOnObject(g16,g9)
    c: Tangent(g12,g15) = -1.5708
    c: Tangent(g9,g15) = -1.5708
    c: PointOnObject(g18,g10)
    c: Tangent(g9,g17) = -1.5708
    c: Tangent(g10,g17) = -1.5708
    c: PointOnObject(g20,g10)
    c: PointOnObject(g20,g11)
    c: Tangent(g10,g19) = -1.5708
    c: Tangent(g11,g19) = -1.5708
    c: PointOnObject(g22,g11)
    c: PointOnObject(g22,g12)
    c: Tangent(g11,g21) = -1.5708
    c: Tangent(g12,g21) = -1.5708
    c: Equal(g15,g17)
    c: Equal(g17,g19)
    c: Equal(g19,g21)
    c: Symmetric(g22,g18,g14)
    c: Radius(g15) = 15
FEATURE [PartDesign::Pad] Pad002
  BaseFeature = -> Pad001
  Direction = (0,-1,2e-16)
  Length = 15
  Length2 = 10
  Profile = -> Sketch002
  ReferenceAxis = -> Sketch002 [N_Axis]
  Suppressed = false
  Type = 0
FEATURE [Sketcher::SketchObject] Sketch003
  ArcFitTolerance = 1e-06
  AttachmentSupport = -> [Pad002]
  ExternalGeometry = -> [Pad002]
  FullyConstrained = false
  MakeInternals = false
  MapMode = 5
  Placement = pos=(0,-234,0) rot=(1,0,0;1.5708rad)
  sketch-geometry (14):
    g0: LineSegment [constr] StartX=-160.058 StartY=332.961 StartZ=0 EndX=-175 EndY=332.961 EndZ=0
    g1: LineSegment [constr] StartX=175 StartY=220.08 StartZ=0 EndX=175 EndY=205.039 EndZ=0
    g2: LineSegment [constr] StartX=160 StartY=205.039 StartZ=0 EndX=175 EndY=205.039 EndZ=0
    g3: LineSegment [constr] StartX=-175 StartY=317.961 StartZ=0 EndX=-175 EndY=332.961 EndZ=0
    g4: LineSegment StartX=-175 StartY=317.961 StartZ=0 EndX=-175 EndY=220.039 EndZ=0
    g5: LineSegment StartX=-160 StartY=205.039 StartZ=0 EndX=160 EndY=205.039 EndZ=0
    g6: LineSegment StartX=175 StartY=220.039 StartZ=0 EndX=175 EndY=317.961 EndZ=0
    g7: LineSegment StartX=160 StartY=332.961 StartZ=0 EndX=-160 EndY=332.961 EndZ=0
    g8: ArcOfCircle CenterX=-160 CenterY=317.961 CenterZ=0 NormalX=0 NormalY=0 NormalZ=1 AngleXU=0 Radius=15 StartAngle=1.5708 EndAngle=3.14159
    g9: ArcOfCircle CenterX=-160 CenterY=220.039 CenterZ=0 NormalX=0 NormalY=0 NormalZ=1 AngleXU=0 Radius=15 StartAngle=3.14159 EndAngle=4.71239
    g10: ArcOfCircle CenterX=160 CenterY=220.039 CenterZ=0 NormalX=0 NormalY=0 NormalZ=1 AngleXU=0 Radius=15 StartAngle=4.71239 EndAngle=6.28319
    g11: ArcOfCircle CenterX=160 CenterY=317.961 CenterZ=0 NormalX=0 NormalY=0 NormalZ=1 AngleXU=0 Radius=15 StartAngle=0 EndAngle=1.5708
    g12: GeomPoint [constr] X=-175 Y=332.961 Z=0
    g13: GeomPoint [constr] X=175 Y=205.039 Z=0
  constraints (30):
    c: Coincident(g2,g-6)
    c: Horizontal(g2)
    c: Vertical(g1)
    c: Coincident(g1,g2)
    c: Coincident(g3,g-4)
    c: Vertical(g3)
    c: Horizontal(g0)
    c: Coincident(g0,g3)
    c: Tangent(g4,g8) = -1.5708
    c: Tangent(g4,g9) = -1.5708
    c: Tangent(g5,g9) = -1.5708
    c: Tangent(g5,g10) = -1.5708
    c: Tangent(g6,g10) = -1.5708
    c: Tangent(g6,g11) = -1.5708
    c: Tangent(g7,g11) = -1.5708
    c: Tangent(g7,g8) = -1.5708
    c: Vertical(g4)
    c: Vertical(g6)
    c: Horizontal(g5)
    c: Horizontal(g7)
    c: Equal(g8,g9)
    c: Equal(g9,g10)
    c: Equal(g10,g11)
    c: PointOnObject(g12,g4)
    c: PointOnObject(g12,g7)
    c: PointOnObject(g13,g5)
    c: PointOnObject(g13,g6)
    c: Radius(g9) = 15
    c: Coincident(g12,g0)
    c: Coincident(g13,g1)
FEATURE [PartDesign::Pad] Pad003
  BaseFeature = -> Pad002
  Direction = (0,-1,2e-16)
  Length = 15
  Length2 = 10
  Profile = -> Sketch003
  ReferenceAxis = -> Sketch003 [N_Axis]
  Suppressed = false
  Type = 0
FEATURE [Sketcher::SketchObject] Sketch004
  ArcFitTolerance = 1e-06
  AttachmentSupport = -> [Pad003]
  ExternalGeometry = -> [Pad003]
  FullyConstrained = false
  MakeInternals = false
  MapMode = 5
  Placement = pos=(0,-249,0) rot=(1,0,0;1.5708rad)
  sketch-geometry (6):
    g0: LineSegment StartX=-111.613 StartY=386.284 StartZ=0 EndX=-111.613 EndY=360.677 EndZ=0
    g1: LineSegment StartX=-111.613 StartY=360.677 StartZ=0 EndX=111.814 EndY=360.677 EndZ=0
    g2: LineSegment StartX=111.814 StartY=360.677 StartZ=0 EndX=111.814 EndY=386.284 EndZ=0
    g3: LineSegment StartX=111.814 StartY=386.284 StartZ=0 EndX=-111.613 EndY=386.284 EndZ=0
    g4: LineSegment [constr] StartX=0.100445 StartY=414 StartZ=0 EndX=0.100445 EndY=332.961 EndZ=0
    g5: LineSegment [constr] StartX=-111.613 StartY=386.284 StartZ=0 EndX=0.100445 EndY=373.481 EndZ=0
  constraints (14):
    c: Coincident(g0,g1)
    c: Coincident(g1,g2)
    c: Coincident(g2,g3)
    c: Coincident(g3,g0)
    c: Vertical(g0)
    c: Vertical(g2)
    c: Horizontal(g1)
    c: Horizontal(g3)
    c: Vertical(g4)
    c: PointOnObject(g4,g-4)
    c: PointOnObject(g4,g-3)
    c: Coincident(g5,g0)
    c: Symmetric(g4,g4,g5)
    c: Symmetric(g0,g2,g5)
FEATURE [PartDesign::Pad] Pad004
  BaseFeature = -> Pad003
  Direction = (0,-1,2e-16)
  Length = 50
  Length2 = 10
  Profile = -> Sketch004
  ReferenceAxis = -> Sketch004 [N_Axis]
  Suppressed = false
  Type = 0
FEATURE [Sketcher::SketchObject] Sketch005
  ArcFitTolerance = 1e-06
  AttachmentSupport = -> [Pad004]
  ExternalGeometry = -> [Pad004]
  FullyConstrained = false
  MakeInternals = false
  MapMode = 5
  Placement = pos=(0,8.5e-14,386.284) rot=(0,0,1;0rad)
  sketch-geometry (13):
    g0: LineSegment StartX=-92.1016 StartY=-250.2 StartZ=0 EndX=-92.1016 EndY=-274.605 EndZ=0
    g1: LineSegment StartX=-82.1016 StartY=-284.605 StartZ=0 EndX=82.1016 EndY=-284.605 EndZ=0
    g2: LineSegment StartX=92.1016 StartY=-274.605 StartZ=0 EndX=92.1016 EndY=-250.713 EndZ=0
    g3: LineSegment StartX=91.1044 StartY=-249.713 StartZ=0 EndX=-91.0988 EndY=-249.2 EndZ=0
    g4: ArcOfCircle CenterX=-82.1016 CenterY=-274.605 CenterZ=0 NormalX=0 NormalY=0 NormalZ=1 AngleXU=0 Radius=10 StartAngle=3.14159 EndAngle=4.71239
    g5: GeomPoint [constr] X=-92.1016 Y=-284.605 Z=0
    g6: ArcOfCircle CenterX=82.1016 CenterY=-274.605 CenterZ=0 NormalX=0 NormalY=0 NormalZ=1 AngleXU=0 Radius=10 StartAngle=4.71239 EndAngle=6.28319
    g7: GeomPoint [constr] X=92.1016 Y=-284.605 Z=0
    g8: ArcOfCircle CenterX=-91.1016 CenterY=-250.2 CenterZ=0 NormalX=0 NormalY=0 NormalZ=1 AngleXU=0 Radius=1 StartAngle=1.56798 EndAngle=3.14159
    g9: GeomPoint [constr] X=-92.1012 Y=-249 Z=0
    g10: ArcOfCircle CenterX=91.1016 CenterY=-250.713 CenterZ=0 NormalX=0 NormalY=0 NormalZ=1 AngleXU=0 Radius=1 StartAngle=7.3e-15 EndAngle=1.56798
    g11: GeomPoint [constr] X=92.1012 Y=-249 Z=0
    g12: LineSegment [constr] StartX=-91.0988 StartY=-249.2 StartZ=0 EndX=-91.0988 EndY=-249 EndZ=0
  constraints (23):
    c: Vertical(g0)
    c: Vertical(g2)
    c: Symmetric(g5,g7,g-2)
    c: PointOnObject(g5,g0)
    c: PointOnObject(g5,g1)
    c: Tangent(g0,g4) = -1.5708
    c: Tangent(g1,g4) = -1.5708
    c: PointOnObject(g7,g1)
    c: PointOnObject(g7,g2)
    c: Tangent(g1,g6) = -1.5708
    c: Tangent(g2,g6) = -1.5708
    c: Equal(g6,g4)
    c: Radius(g6) = 10
    c: Tangent(g3,g8) = -1.5708
    c: Tangent(g0,g8) = -1.5708
    c: Tangent(g3,g10) = -1.5708
    c: Tangent(g2,g10) = -1.5708
    c: Equal(g10,g8)
    c: Radius(g10) = 1
    c: Coincident(g12,g3)
    c: Vertical(g12)
    c: PointOnObject(g12,g-3)
    c: DistanceY(g12,g12) = 0.2
FEATURE [PartDesign::Pocket] Pocket
  BaseFeature = -> Pad004
  Direction = (0,0,-1)
  Length = 5
  Length2 = 5
  Profile = -> Sketch005
  ReferenceAxis = -> Sketch005 [N_Axis]
  Suppressed = false
  Type = 1
FEATURE [Sketcher::SketchObject] Sketch006
  ArcFitTolerance = 1e-06
  AttachmentSupport = -> [Pocket]
  ExternalGeometry = -> [Pocket]
  FullyConstrained = false
  MakeInternals = false
  MapMode = 5
  Placement = pos=(0,-249,0) rot=(1,0,0;1.5708rad)
  sketch-geometry (4):
    g0: Circle CenterX=162.576 CenterY=66.5 CenterZ=0 NormalX=0 NormalY=0 NormalZ=1 AngleXU=0 Radius=35
    g1: Circle CenterX=18.3518 CenterY=66.5 CenterZ=0 NormalX=0 NormalY=0 NormalZ=1 AngleXU=0 Radius=35
    g2: LineSegment [constr] StartX=18.3518 StartY=66.5 StartZ=0 EndX=18.3518 EndY=119 EndZ=0
    g3: LineSegment [constr] StartX=18.3518 StartY=66.5 StartZ=0 EndX=18.3518 EndY=14 EndZ=0
  constraints (9):
    c: Equal(g0,g1)
    c: Radius(g1) = 35
    c: Coincident(g2,g1)
    c: Vertical(g2)
    c: Coincident(g3,g1)
    c: PointOnObject(g2,g-3)
    c: PointOnObject(g3,g-4)
    c: Symmetric(g2,g3,g1)
    c: Horizontal(g0,g1)
FEATURE [PartDesign::Pocket] Pocket001
  BaseFeature = -> Pocket
  Direction = (0,1,-2e-16)
  Length = 14
  Length2 = 5
  Profile = -> Sketch006
  ReferenceAxis = -> Sketch006 [N_Axis]
  Suppressed = false
  Type = 0
FEATURE [Sketcher::SketchObject] Sketch007
  ArcFitTolerance = 1e-06
  AttachmentSupport = -> [Pocket001]
  ExternalGeometry = -> [Pocket001]
  FullyConstrained = true
  MakeInternals = false
  MapMode = 5
  Placement = pos=(0,-235,1.105e-13) rot=(1,0,0;1.5708rad)
  sketch-geometry (2):
    g0: Circle CenterX=18.3518 CenterY=66.5 CenterZ=0 NormalX=0 NormalY=0 NormalZ=1 AngleXU=0 Radius=30
    g1: Circle CenterX=162.576 CenterY=66.5 CenterZ=0 NormalX=0 NormalY=0 NormalZ=1 AngleXU=0 Radius=30
  constraints (4):
    c: Diameter(g0) = 60
    c: Coincident(g0,g-3)
    c: Diameter(g1) = 60
    c: Coincident(g1,g-4)
FEATURE [PartDesign::Pad] Pad005
  BaseFeature = -> Pocket001
  Direction = (0,-1,2e-16)
  Length = 15
  Length2 = 10
  Profile = -> Sketch007
  ReferenceAxis = -> Sketch007 [N_Axis]
  Suppressed = false
  Type = 0
FEATURE [Sketcher::SketchObject] Sketch008
  ArcFitTolerance = 1e-06
  AttachmentSupport = -> [Pad005]
  ExternalGeometry = -> [Pad005]
  FullyConstrained = false
  MakeInternals = false
  MapMode = 5
  Placement = pos=(0,-250,1.375e-13) rot=(1,0,0;1.5708rad)
  sketch-geometry (8):
    g0: ArcOfCircle CenterX=18.3518 CenterY=89.5 CenterZ=0 NormalX=0 NormalY=0 NormalZ=1 AngleXU=0 Radius=5.5429 StartAngle=1.2e-15 EndAngle=3.14159
    g1: ArcOfCircle CenterX=18.3518 CenterY=43.5 CenterZ=0 NormalX=0 NormalY=0 NormalZ=1 AngleXU=0 Radius=5.5429 StartAngle=3.14159 EndAngle=6.28319
    g2: LineSegment StartX=23.8947 StartY=89.5 StartZ=0 EndX=23.8947 EndY=43.5 EndZ=0
    g3: LineSegment StartX=12.8089 StartY=89.5 StartZ=0 EndX=12.8089 EndY=43.5 EndZ=0
    g4: ArcOfCircle CenterX=162.576 CenterY=89.5 CenterZ=0 NormalX=0 NormalY=0 NormalZ=1 AngleXU=0 Radius=5.5429 StartAngle=-9e-16 EndAngle=3.14159
    g5: ArcOfCircle CenterX=162.576 CenterY=43.5 CenterZ=0 NormalX=0 NormalY=0 NormalZ=1 AngleXU=0 Radius=5.5429 StartAngle=3.14159 EndAngle=6.28319
    g6: LineSegment StartX=168.119 StartY=89.5 StartZ=0 EndX=168.119 EndY=43.5 EndZ=0
    g7: LineSegment StartX=157.033 StartY=89.5 StartZ=0 EndX=157.033 EndY=43.5 EndZ=0
  constraints (17):
    c: Tangent(g0,g2) = 1.5708
    c: Tangent(g0,g3) = -1.5708
    c: Tangent(g1,g2) = 1.5708
    c: Tangent(g1,g3) = -1.5708
    c: Equal(g0,g1)
    c: Vertical(g2)
    c: Tangent(g4,g6) = 1.5708
    c: Tangent(g4,g7) = -1.5708
    c: Tangent(g5,g6) = 1.5708
    c: Tangent(g5,g7) = -1.5708
    c: Equal(g4,g5)
    c: Symmetric(g0,g1,g-3)
    c: Symmetric(g4,g5,g-4)
    c: Vertical(g4,g5)
    c: Equal(g7,g3)
    c: Equal(g0,g4)
    c: DistanceY(g3,g3) = 46
FEATURE [PartDesign::Pad] Pad006
  BaseFeature = -> Pad005
  Direction = (0,-1,2e-16)
  Length = 15
  Length2 = 10
  Profile = -> Sketch008
  ReferenceAxis = -> Sketch008 [N_Axis]
  Suppressed = false
  Type = 0
FEATURE [Sketcher::SketchObject] Sketch009
  ArcFitTolerance = 1e-06
  AttachmentSupport = -> [Pad001]
  FullyConstrained = false
  MakeInternals = false
  MapMode = 5
  Placement = pos=(0,-234,0) rot=(1,0,0;1.5708rad)
  sketch-geometry (4):
    g0: LineSegment StartX=-227.24 StartY=377.791 StartZ=0 EndX=-227.24 EndY=190.77 EndZ=0
    g1: LineSegment StartX=-227.24 StartY=190.77 StartZ=0 EndX=227.24 EndY=190.77 EndZ=0
    g2: LineSegment StartX=227.24 StartY=190.77 StartZ=0 EndX=227.24 EndY=377.791 EndZ=0
    g3: LineSegment StartX=227.24 StartY=377.791 StartZ=0 EndX=-227.24 EndY=377.791 EndZ=0
  constraints (8):
    c: Coincident(g0,g1)
    c: Coincident(g1,g2)
    c: Coincident(g2,g3)
    c: Coincident(g3,g0)
    c: Vertical(g0)
    c: Vertical(g2)
    c: Horizontal(g1)
    c: Symmetric(g0,g2,g-2)
FEATURE [PartDesign::Pocket] Pocket002
  BaseFeature = -> Pad006
  Direction = (0,1,-2e-16)
  Length = 450
  Length2 = 5
  Profile = -> Sketch009
  ReferenceAxis = -> Sketch009 [N_Axis]
  Suppressed = false
  Type = 0
FEATURE [PartDesign::Fillet] Fillet
  Base = -> Pocket002 [Edge13,Edge14]
  BaseFeature = -> Pocket002
  Radius = 3
  SupportTransform = false
  Suppressed = false
  UseAllEdges = false
FEATURE [PartDesign::Fillet] Fillet001
  Base = -> Fillet [Edge45,Edge38]
  BaseFeature = -> Fillet
  Radius = 40
  SupportTransform = false
  Suppressed = false
  UseAllEdges = false
FEATURE [PartDesign::Fillet] Fillet002
  Base = -> Fillet001 [Edge79,Edge80]
  BaseFeature = -> Fillet001
  Radius = 5
  SupportTransform = false
  Suppressed = false
  UseAllEdges = false
FEATURE [PartDesign::Fillet] Fillet003
  Base = -> Fillet002 [Edge74,Edge94]
  BaseFeature = -> Fillet002
  Radius = 2
  SupportTransform = false
  Suppressed = false
  UseAllEdges = false
FEATURE [PartDesign::Fillet] Fillet004
  Base = -> Fillet003 [Edge33,Edge181]
  BaseFeature = -> Fillet003
  Radius = 3
  SupportTransform = false
  Suppressed = false
  UseAllEdges = false
FEATURE [PartDesign::Fillet] Fillet005
  Base = -> Fillet004 [Edge158,Edge147]
  BaseFeature = -> Fillet004
  Radius = 10
  SupportTransform = false
  Suppressed = false
  UseAllEdges = false
FEATURE [PartDesign::Fillet] Fillet006
  Base = -> Fillet005 [Edge4]
  BaseFeature = -> Fillet005
  Radius = 5
  SupportTransform = false
  Suppressed = false
  UseAllEdges = false
FEATURE [PartDesign::Fillet] Fillet007
  Base = -> Fillet006 [Edge14]
  BaseFeature = -> Fillet006
  Radius = 5
  SupportTransform = false
  Suppressed = false
  UseAllEdges = false
FEATURE [Sketcher::SketchObject] Sketch010
  ArcFitTolerance = 1e-06
  AttachmentSupport = -> [Fillet007]
  ExternalGeometry = -> [Fillet007]
  FullyConstrained = false
  MakeInternals = false
  MapMode = 5
  Placement = pos=(0,-249,0) rot=(1,0,0;1.5708rad)
  sketch-geometry (14):
    g0: LineSegment [constr] StartX=-160 StartY=332.961 StartZ=0 EndX=-175 EndY=332.961 EndZ=0
    g1: LineSegment [constr] StartX=-175 StartY=317.961 StartZ=0 EndX=-175 EndY=332.961 EndZ=0
    g2: LineSegment [constr] StartX=175 StartY=220.039 StartZ=0 EndX=175 EndY=205.039 EndZ=0
    g3: LineSegment [constr] StartX=160 StartY=205.039 StartZ=0 EndX=175 EndY=205.039 EndZ=0
    g4: LineSegment StartX=-175 StartY=317.961 StartZ=0 EndX=-175 EndY=220.039 EndZ=0
    g5: LineSegment StartX=-160 StartY=205.039 StartZ=0 EndX=160 EndY=205.039 EndZ=0
    g6: LineSegment StartX=175 StartY=220.039 StartZ=0 EndX=175 EndY=317.961 EndZ=0
    g7: LineSegment StartX=160 StartY=332.961 StartZ=0 EndX=-160 EndY=332.961 EndZ=0
    g8: ArcOfCircle CenterX=-160 CenterY=317.961 CenterZ=0 NormalX=0 NormalY=0 NormalZ=1 AngleXU=0 Radius=15 StartAngle=1.5708 EndAngle=3.14159
    g9: ArcOfCircle CenterX=-160 CenterY=220.039 CenterZ=0 NormalX=0 NormalY=0 NormalZ=1 AngleXU=0 Radius=15 StartAngle=3.14159 EndAngle=4.71239
    g10: ArcOfCircle CenterX=160 CenterY=220.039 CenterZ=0 NormalX=0 NormalY=0 NormalZ=1 AngleXU=0 Radius=15 StartAngle=4.71239 EndAngle=6.28319
    g11: ArcOfCircle CenterX=160 CenterY=317.961 CenterZ=0 NormalX=0 NormalY=0 NormalZ=1 AngleXU=0 Radius=15 StartAngle=0 EndAngle=1.5708
    g12: GeomPoint [constr] X=-175 Y=332.961 Z=0
    g13: GeomPoint [constr] X=175 Y=205.039 Z=0
  constraints (31):
    c: Coincident(g0,g-3)
    c: Horizontal(g0)
    c: Coincident(g1,g-4)
    c: Vertical(g1)
    c: Coincident(g0,g1)
    c: Coincident(g2,g-5)
    c: Vertical(g2)
    c: Coincident(g3,g-6)
    c: Horizontal(g3)
    c: Coincident(g2,g3)
    c: Tangent(g4,g8) = -1.5708
    c: Tangent(g4,g9) = -1.5708
    c: Tangent(g5,g9) = -1.5708
    c: Tangent(g5,g10) = -1.5708
    c: Tangent(g6,g10) = -1.5708
    c: Tangent(g6,g11) = -1.5708
    c: Tangent(g7,g11) = -1.5708
    c: Tangent(g7,g8) = -1.5708
    c: Vertical(g4)
    c: Vertical(g6)
    c: Horizontal(g5)
    c: Horizontal(g7)
    c: Equal(g8,g9)
    c: Equal(g9,g10)
    c: Equal(g10,g11)
    c: PointOnObject(g12,g4)
    c: PointOnObject(g12,g7)
    c: PointOnObject(g13,g5)
    c: PointOnObject(g13,g6)
    c: Coincident(g12,g0)
    c: Coincident(g13,g2)
FEATURE [PartDesign::Pocket] Pocket003
  BaseFeature = -> Fillet007
  Direction = (0,1,-2e-16)
  Length = 30
  Length2 = 5
  Profile = -> Sketch010
  ReferenceAxis = -> Sketch010 [N_Axis]
  Refine = true
  Suppressed = false
  Type = 0
FEATURE [PartDesign::ShapeBinder] CopyPocket003
  Placement = pos=(0,-235,1.1e-13) rot=(1,0,0;1.5708rad)
  TraceSupport = false
FEATURE [PartDesign::Plane] DatumPlane
  AttachmentSupport = -> [CopyPocket003]
  Length = 105.028
  MapMode = 11
  Placement = pos=(18.3518,-235,66.5) rot=(0.57735,-0.57735,0.57735;2.0944rad)
  ResizeMode = 0
  Width = 63.5277
FEATURE [Sketcher::SketchObject] Sketch011
  ArcFitTolerance = 1e-06
  AttachmentSupport = -> [DatumPlane]
  ExternalGeometry = -> [CopyPocket003]
  FullyConstrained = false
  MakeInternals = false
  MapMode = 5
  Placement = pos=(18.3518,-235,66.5) rot=(0.57735,-0.57735,0.57735;2.0944rad)
  sketch-geometry (1):
    g0: Circle CenterX=0 CenterY=0 CenterZ=0 NormalX=0 NormalY=0 NormalZ=1 AngleXU=0 Radius=30
  constraints (1):
    c: Coincident(g0,g-1)
FEATURE [PartDesign::Pad] Pad007
  Direction = (0,-1,0)
  Length = 15
  Length2 = 10
  Placement = pos=(18.3518,-235,66.5) rot=(0.57735,-0.57735,0.57735;2.0944rad)
  Profile = -> Sketch011
  ReferenceAxis = -> Sketch011 [N_Axis]
  Refine = true
  Suppressed = false
  Type = 0
FEATURE [PartDesign::ShapeBinder] CopyPocket004
  Placement = pos=(0,-250,1.37e-13) rot=(1,0,0;1.5708rad)
  TraceSupport = false
FEATURE [PartDesign::Line] DatumLine
  AttacherType = Attacher::AttachEngineLine
  AttachmentSupport = -> [CopyPocket004]
  Length = 20
  MapMode = 29
  Placement = pos=(12.8089,-250,1.421e-13) rot=(0,1,0;3.14159rad)
  ResizeMode = 0
FEATURE [PartDesign::ShapeBinder] CopyPocket005
  TraceSupport = false
FEATURE [PartDesign::Line] DatumLine001
  AttacherType = Attacher::AttachEngineLine
  AttachmentSupport = -> [CopyPocket005]
  Length = 20
  MapMode = 19
  Placement = pos=(18.3518,-262,89.5) rot=(0,0.707107,0.707107;3.14159rad)
  ResizeMode = 0
FEATURE [PartDesign::ShapeBinder] CopyPocket006
  TraceSupport = false
FEATURE [PartDesign::Line] DatumLine002
  AttacherType = Attacher::AttachEngineLine
  AttachmentSupport = -> [CopyPocket006]
  Length = 20
  MapMode = 19
  Placement = pos=(18.3518,-262,43.5) rot=(-1,0,0;1.5708rad)
  ResizeMode = 0
FEATURE [PartDesign::ShapeBinder] CopyPocket007
  Placement = pos=(0,-250,1.37e-13) rot=(1,0,0;1.5708rad)
  TraceSupport = false
FEATURE [PartDesign::Line] DatumLine003
  AttacherType = Attacher::AttachEngineLine
  AttachmentSupport = -> [CopyPocket007]
  Length = 20
  MapMode = 29
  Placement = pos=(23.8947,-250,1.421e-13) rot=(0,1,0;3.14159rad)
  ResizeMode = 0
FEATURE [Sketcher::SketchObject] Sketch012
  ArcFitTolerance = 1e-06
  AttachmentSupport = -> [Pad007]
  ExternalGeometry = -> [DatumLine,DatumLine003,CopyPocket005,CopyPocket006]
  FullyConstrained = false
  MakeInternals = false
  MapMode = 5
  Placement = pos=(18.3518,-250,66.5) rot=(0.57735,-0.57735,0.57735;2.0944rad)
  sketch-geometry (4):
    g0: ArcOfCircle CenterX=-23 CenterY=-1.851e-13 CenterZ=0 NormalX=0 NormalY=0 NormalZ=1 AngleXU=0 Radius=5.5429 StartAngle=1.5708 EndAngle=4.71239
    g1: ArcOfCircle CenterX=23 CenterY=-1.851e-13 CenterZ=0 NormalX=0 NormalY=0 NormalZ=1 AngleXU=0 Radius=5.5429 StartAngle=4.71239 EndAngle=7.85398
    g2: LineSegment StartX=-23 StartY=5.5429 StartZ=0 EndX=23 EndY=5.5429 EndZ=0
    g3: LineSegment StartX=-23 StartY=-5.5429 StartZ=0 EndX=23 EndY=-5.5429 EndZ=0
  constraints (6):
    c: Tangent(g0,g2) = 1.5708
    c: Tangent(g0,g3) = -1.5708
    c: Tangent(g1,g2) = 1.5708
    c: Tangent(g1,g3) = -1.5708
    c: Equal(g0,g1)
    c: Horizontal(g3)
FEATURE [PartDesign::Pad] Pad008
  BaseFeature = -> Pad007
  Direction = (0,-1,0)
  Length = 15
  Length2 = 10
  Placement = pos=(18.3518,-235,66.5) rot=(0.57735,-0.57735,0.57735;2.0944rad)
  Profile = -> Sketch012
  ReferenceAxis = -> Sketch012 [N_Axis]
  Refine = true
  Suppressed = false
  Type = 0
FEATURE [PartDesign::Fillet] Fillet008
  Base = -> Pad008 [Edge3]
  BaseFeature = -> Pad008
  Placement = pos=(18.3518,-235,66.5) rot=(0.57735,-0.57735,0.57735;2.0944rad)
  Radius = 2
  Refine = true
  SupportTransform = false
  Suppressed = false
  UseAllEdges = false
FEATURE [PartDesign::Fillet] Fillet009
  Base = -> Fillet008 [Edge31]
  BaseFeature = -> Fillet008
  Placement = pos=(18.3518,-235,66.5) rot=(0.57735,-0.57735,0.57735;2.0944rad)
  Radius = 3
  Refine = true
  SupportTransform = false
  Suppressed = false
  UseAllEdges = false
FEATURE [PartDesign::Body] Body001
  AllowCompound = false
  Group = -> [DatumPlane,CopyPocket003,Sketch011,Pad007,DatumLine,CopyPocket004,DatumLine001,CopyPocket005,DatumLine002,CopyPocket006,DatumLine003,CopyPocket007,Sketch012,Pad008,Fillet008,Fillet009]
  Origin = -> Origin001
  Tip = -> Fillet009
FEATURE [PartDesign::ShapeBinder] CopyPocket008
  Placement = pos=(0,-235,1.1e-13) rot=(1,0,0;1.5708rad)
  TraceSupport = false
FEATURE [PartDesign::Plane] DatumPlane001
  AttachmentSupport = -> [CopyPocket008]
  Length = 117.702
  MapMode = 11
  Placement = pos=(162.576,-235,66.5) rot=(0.57735,-0.57735,0.57735;2.0944rad)
  ResizeMode = 0
  Width = 213.778
FEATURE [PartDesign::ShapeBinder] CopyPocket009
  TraceSupport = false
FEATURE [PartDesign::Line] DatumLine004
  AttacherType = Attacher::AttachEngineLine
  AttachmentSupport = -> [CopyPocket009]
  Length = 20
  MapMode = 29
  Placement = pos=(157.033,-262,0) rot=(0,0,1;0rad)
  ResizeMode = 0
FEATURE [PartDesign::ShapeBinder] CopyPocket010
  TraceSupport = false
FEATURE [PartDesign::Line] DatumLine005
  AttacherType = Attacher::AttachEngineLine
  AttachmentSupport = -> [CopyPocket010]
  Length = 20
  MapMode = 19
  Placement = pos=(162.576,-262,89.5) rot=(0,0.707107,0.707107;3.14159rad)
  ResizeMode = 0
FEATURE [PartDesign::ShapeBinder] CopyPocket011
  TraceSupport = false
FEATURE [PartDesign::Line] DatumLine006
  AttacherType = Attacher::AttachEngineLine
  AttachmentSupport = -> [CopyPocket011]
  Length = 20
  MapMode = 29
  Placement = pos=(168.119,-262,0) rot=(0,1,0;3.14159rad)
  ResizeMode = 0
FEATURE [PartDesign::ShapeBinder] CopyPocket012
  TraceSupport = false
FEATURE [PartDesign::Line] DatumLine007
  AttacherType = Attacher::AttachEngineLine
  AttachmentSupport = -> [CopyPocket012]
  Length = 20
  MapMode = 19
  Placement = pos=(162.576,-262,43.5) rot=(-1,0,0;1.5708rad)
  ResizeMode = 0
FEATURE [Sketcher::SketchObject] Sketch013
  ArcFitTolerance = 1e-06
  AttachmentSupport = -> [DatumPlane001]
  ExternalGeometry = -> [CopyPocket008]
  FullyConstrained = false
  MakeInternals = false
  MapMode = 5
  Placement = pos=(162.576,-235,66.5) rot=(0.57735,-0.57735,0.57735;2.0944rad)
  sketch-geometry (1):
    g0: Circle CenterX=0 CenterY=0 CenterZ=0 NormalX=0 NormalY=0 NormalZ=1 AngleXU=0 Radius=30
  constraints (1):
    c: Coincident(g0,g-1)
FEATURE [PartDesign::Pad] Pad009
  Direction = (0,-1,0)
  Length = 15
  Length2 = 10
  Placement = pos=(162.576,-235,66.5) rot=(0.57735,-0.57735,0.57735;2.0944rad)
  Profile = -> Sketch013
  ReferenceAxis = -> Sketch013 [N_Axis]
  Refine = true
  Suppressed = false
  Type = 0
FEATURE [Sketcher::SketchObject] Sketch014
  ArcFitTolerance = 1e-06
  AttachmentSupport = -> [Pad009]
  ExternalGeometry = -> [DatumLine004,DatumLine006,CopyPocket012,CopyPocket010]
  FullyConstrained = false
  MakeInternals = false
  MapMode = 5
  Placement = pos=(162.576,-250,66.5) rot=(0.57735,-0.57735,0.57735;2.0944rad)
  sketch-geometry (4):
    g0: ArcOfCircle CenterX=-23 CenterY=-3.707e-13 CenterZ=0 NormalX=0 NormalY=0 NormalZ=1 AngleXU=0 Radius=5.5429 StartAngle=1.5708 EndAngle=4.71239
    g1: ArcOfCircle CenterX=23 CenterY=-3.707e-13 CenterZ=0 NormalX=0 NormalY=0 NormalZ=1 AngleXU=0 Radius=5.5429 StartAngle=4.71239 EndAngle=7.85398
    g2: LineSegment StartX=-23 StartY=5.5429 StartZ=0 EndX=23 EndY=5.5429 EndZ=0
    g3: LineSegment StartX=-23 StartY=-5.5429 StartZ=0 EndX=23 EndY=-5.5429 EndZ=0
  constraints (6):
    c: Tangent(g0,g2) = 1.5708
    c: Tangent(g0,g3) = -1.5708
    c: Tangent(g1,g2) = 1.5708
    c: Tangent(g1,g3) = -1.5708
    c: Equal(g0,g1)
    c: Horizontal(g3)
FEATURE [PartDesign::Pad] Pad010
  BaseFeature = -> Pad009
  Direction = (0,-1,0)
  Length = 15
  Length2 = 10
  Placement = pos=(162.576,-235,66.5) rot=(0.57735,-0.57735,0.57735;2.0944rad)
  Profile = -> Sketch014
  ReferenceAxis = -> Sketch014 [N_Axis]
  Refine = true
  Suppressed = false
  Type = 0
FEATURE [PartDesign::Fillet] Fillet010
  Base = -> Pad010 [Edge3]
  BaseFeature = -> Pad010
  Placement = pos=(162.576,-235,66.5) rot=(0.57735,-0.57735,0.57735;2.0944rad)
  Radius = 2
  Refine = true
  SupportTransform = false
  Suppressed = false
  UseAllEdges = false
FEATURE [PartDesign::Fillet] Fillet011
  Base = -> Fillet010 [Edge30]
  BaseFeature = -> Fillet010
  Placement = pos=(162.576,-235,66.5) rot=(0.57735,-0.57735,0.57735;2.0944rad)
  Radius = 3
  Refine = true
  SupportTransform = false
  Suppressed = false
  UseAllEdges = false
FEATURE [PartDesign::Body] Body002
  AllowCompound = false
  Group = -> [DatumPlane001,CopyPocket008,DatumLine004,CopyPocket009,DatumLine005,CopyPocket010,DatumLine006,CopyPocket011,DatumLine007,CopyPocket012,Sketch013,Pad009,Sketch014,Pad010,Fillet010,Fillet011]
  Origin = -> Origin002
  Tip = -> Fillet011
FEATURE [Sketcher::SketchObject] Sketch015
  ArcFitTolerance = 1e-06
  AttachmentSupport = -> [Pocket003]
  ExternalGeometry = -> [Pocket003]
  FullyConstrained = false
  MakeInternals = false
  MapMode = 5
  Placement = pos=(0,-265,1.564e-13) rot=(1,0,0;1.5708rad)
  sketch-geometry (1):
    g0: Circle CenterX=18.3518 CenterY=66.5 CenterZ=0 NormalX=0 NormalY=0 NormalZ=1 AngleXU=0 Radius=30
  constraints (1):
    c: Coincident(g0,g-4)
FEATURE [PartDesign::Pocket] Pocket004
  BaseFeature = -> Pocket003
  Direction = (0,1,-2e-16)
  Length = 30
  Length2 = 5
  Profile = -> Sketch015
  ReferenceAxis = -> Sketch015 [N_Axis]
  Refine = true
  Suppressed = false
  Type = 0
FEATURE [Sketcher::SketchObject] Sketch016
  ArcFitTolerance = 1e-06
  AttachmentSupport = -> [Pocket004]
  ExternalGeometry = -> [Pocket004]
  FullyConstrained = true
  MakeInternals = false
  MapMode = 5
  Placement = pos=(0,-265,1.564e-13) rot=(1,0,0;1.5708rad)
  sketch-geometry (1):
    g0: Circle CenterX=162.576 CenterY=66.5 CenterZ=0 NormalX=0 NormalY=0 NormalZ=1 AngleXU=0 Radius=30
  constraints (2):
    c: Coincident(g0,g-3)
    c: Equal(g0,g-3)
FEATURE [PartDesign::Pocket] Pocket005
  BaseFeature = -> Pocket004
  Direction = (0,1,-2e-16)
  Length = 30
  Length2 = 5
  Profile = -> Sketch016
  ReferenceAxis = -> Sketch016 [N_Axis]
  Refine = true
  Suppressed = false
  Type = 0
FEATURE [PartDesign::ShapeBinder] CopyPocket013
  TraceSupport = false
FEATURE [Sketcher::SketchObject] Sketch017
  ArcFitTolerance = 1e-06
  AttachmentSupport = -> [CopyPocket013]
  ExternalGeometry = -> [CopyPocket013]
  FullyConstrained = false
  MakeInternals = false
  MapMode = 5
  Placement = pos=(0,-249,0) rot=(1,0,0;1.5708rad)
  sketch-geometry (14):
    g0: LineSegment [constr] StartX=-160 StartY=332.961 StartZ=0 EndX=-175 EndY=332.895 EndZ=0
    g1: LineSegment [constr] StartX=-175 StartY=317.961 StartZ=0 EndX=-175 EndY=332.895 EndZ=0
    g2: LineSegment [constr] StartX=174.86 StartY=220.039 StartZ=0 EndX=174.86 EndY=205.023 EndZ=0
    g3: LineSegment [constr] StartX=160 StartY=205.039 StartZ=0 EndX=174.86 EndY=205.023 EndZ=0
    g4: LineSegment StartX=-175 StartY=318.234 StartZ=0 EndX=-175 EndY=219.685 EndZ=0
    g5: LineSegment StartX=-160.339 StartY=205.023 StartZ=0 EndX=160.199 EndY=205.023 EndZ=0
    g6: LineSegment StartX=174.86 StartY=219.685 StartZ=0 EndX=174.86 EndY=318.234 EndZ=0
    g7: LineSegment StartX=160.199 StartY=332.895 StartZ=0 EndX=-160.339 EndY=332.895 EndZ=0
    g8: ArcOfCircle CenterX=-160.339 CenterY=318.234 CenterZ=0 NormalX=0 NormalY=0 NormalZ=1 AngleXU=0 Radius=14.6613 StartAngle=1.5708 EndAngle=3.14159
    g9: ArcOfCircle CenterX=-160.339 CenterY=219.685 CenterZ=0 NormalX=0 NormalY=0 NormalZ=1 AngleXU=0 Radius=14.6613 StartAngle=3.14159 EndAngle=4.71239
    g10: ArcOfCircle CenterX=160.199 CenterY=219.685 CenterZ=0 NormalX=0 NormalY=0 NormalZ=1 AngleXU=0 Radius=14.6613 StartAngle=4.71239 EndAngle=6.28319
    g11: ArcOfCircle CenterX=160.199 CenterY=318.234 CenterZ=0 NormalX=0 NormalY=0 NormalZ=1 AngleXU=0 Radius=14.6613 StartAngle=0 EndAngle=1.5708
    g12: GeomPoint [constr] X=-175 Y=332.895 Z=0
    g13: GeomPoint [constr] X=174.86 Y=205.023 Z=0
  constraints (24):
    c: Coincident(g1,g-4)
    c: Vertical(g1)
    c: Coincident(g0,g1)
    c: Vertical(g2)
    c: PointOnObject(g2,g3)
    c: Tangent(g4,g8) = -1.5708
    c: Tangent(g4,g9) = -1.5708
    c: Tangent(g5,g9) = -1.5708
    c: Tangent(g5,g10) = -1.5708
    c: Tangent(g6,g10) = -1.5708
    c: Tangent(g6,g11) = -1.5708
    c: Tangent(g7,g11) = -1.5708
    c: Tangent(g7,g8) = -1.5708
    c: Vertical(g4)
    c: Vertical(g6)
    c: Horizontal(g5)
    c: Horizontal(g7)
    c: Equal(g8,g9)
    c: Equal(g9,g10)
    c: Equal(g10,g11)
    c: PointOnObject(g12,g4)
    c: PointOnObject(g12,g7)
    c: PointOnObject(g13,g5)
    c: PointOnObject(g13,g6)
FEATURE [PartDesign::Pad] Pad011
  Direction = (0,-1,2e-16)
  Length = 15
  Length2 = 10
  Profile = -> Sketch017
  ReferenceAxis = -> Sketch017 [N_Axis]
  Refine = true
  Reversed = true
  Suppressed = false
  Type = 0
FEATURE [PartDesign::Body] Body003
  AllowCompound = false
  Group = -> [CopyPocket013,Sketch017,Pad011]
  Origin = -> Origin003
  Tip = -> Pad011
FEATURE [PartDesign::ShapeBinder] CopyPocket014
  TraceSupport = false
FEATURE [Sketcher::SketchObject] Sketch018
  ArcFitTolerance = 1e-06
  AttachmentSupport = -> [CopyPocket014]
  ExternalGeometry = -> [CopyPocket014]
  FullyConstrained = false
  MakeInternals = false
  MapMode = 5
  Placement = pos=(0,-249,0) rot=(1,0,0;1.5708rad)
  sketch-geometry (12):
    g0: LineSegment [constr] StartX=-106.613 StartY=386.284 StartZ=0 EndX=-111.613 EndY=386.284 EndZ=0
    g1: LineSegment [constr] StartX=-111.613 StartY=381.284 StartZ=0 EndX=-111.613 EndY=386.284 EndZ=0
    g2: LineSegment StartX=-111.613 StartY=381.284 StartZ=0 EndX=-111.613 EndY=365.677 EndZ=0
    g3: LineSegment StartX=-106.613 StartY=360.677 StartZ=0 EndX=106.814 EndY=360.677 EndZ=0
    g4: LineSegment StartX=111.814 StartY=365.677 StartZ=0 EndX=111.814 EndY=381.284 EndZ=0
    g5: LineSegment StartX=106.814 StartY=386.284 StartZ=0 EndX=-106.613 EndY=386.284 EndZ=0
    g6: ArcOfCircle CenterX=-106.613 CenterY=381.284 CenterZ=0 NormalX=0 NormalY=0 NormalZ=1 AngleXU=0 Radius=5 StartAngle=1.5708 EndAngle=3.14159
    g7: ArcOfCircle CenterX=-106.613 CenterY=365.677 CenterZ=0 NormalX=0 NormalY=0 NormalZ=1 AngleXU=0 Radius=5 StartAngle=3.14159 EndAngle=4.71239
    g8: ArcOfCircle CenterX=106.814 CenterY=365.677 CenterZ=0 NormalX=0 NormalY=0 NormalZ=1 AngleXU=0 Radius=5 StartAngle=4.71239 EndAngle=6.28319
    g9: ArcOfCircle CenterX=106.814 CenterY=381.284 CenterZ=0 NormalX=0 NormalY=0 NormalZ=1 AngleXU=0 Radius=5 StartAngle=0 EndAngle=1.5708
    g10: GeomPoint [constr] X=-111.613 Y=386.284 Z=0
    g11: GeomPoint [constr] X=111.814 Y=360.677 Z=0
  constraints (25):
    c: Coincident(g0,g-3)
    c: Horizontal(g0)
    c: Tangent(g1,g-3) = 1.5708
    c: Coincident(g1,g0)
    c: Tangent(g2,g6) = -1.5708
    c: Tangent(g2,g7) = -1.5708
    c: Tangent(g3,g7) = -1.5708
    c: Tangent(g3,g8) = -1.5708
    c: Tangent(g4,g8) = -1.5708
    c: Tangent(g4,g9) = -1.5708
    c: Tangent(g5,g9) = -1.5708
    c: Tangent(g5,g6) = -1.5708
    c: Vertical(g2)
    c: Vertical(g4)
    c: Horizontal(g3)
    c: Horizontal(g5)
    c: Equal(g6,g7)
    c: Equal(g7,g8)
    c: Equal(g8,g9)
    c: PointOnObject(g10,g2)
    c: PointOnObject(g10,g5)
    c: PointOnObject(g11,g3)
    c: PointOnObject(g11,g4)
    c: Coincident(g10,g0)
    c: Coincident(g11,g-5)
FEATURE [Sketcher::SketchObject] Sketch019
  ArcFitTolerance = 1e-06
  AttachmentSupport = -> [Pocket005]
  ExternalGeometry = -> [Pocket005]
  FullyConstrained = false
  MakeInternals = false
  MapMode = 5
  Placement = pos=(0,-299,0) rot=(1,0,0;1.5708rad)
  sketch-geometry (4):
    g0: LineSegment StartX=-111.613 StartY=360.677 StartZ=0 EndX=113.773 EndY=360.677 EndZ=0
    g1: LineSegment StartX=113.773 StartY=360.677 StartZ=0 EndX=113.773 EndY=391.257 EndZ=0
    g2: LineSegment StartX=113.773 StartY=391.257 StartZ=0 EndX=-111.613 EndY=391.257 EndZ=0
    g3: LineSegment StartX=-111.613 StartY=391.257 StartZ=0 EndX=-111.613 EndY=360.677 EndZ=0
  constraints (9):
    c: Coincident(g0,g1)
    c: Coincident(g1,g2)
    c: Coincident(g2,g3)
    c: Coincident(g3,g0)
    c: Horizontal(g0)
    c: Horizontal(g2)
    c: Vertical(g1)
    c: Vertical(g3)
    c: Coincident(g0,g-4)
FEATURE [PartDesign::Pocket] Pocket006
  BaseFeature = -> Pocket005
  Direction = (0,1,-2e-16)
  Length = 50
  Length2 = 5
  Profile = -> Sketch019
  ReferenceAxis = -> Sketch019 [N_Axis]
  Refine = true
  Suppressed = false
  Type = 0
FEATURE [PartDesign::Pad] Pad012
  Direction = (0,-1,2e-16)
  Length = 50
  Length2 = 10
  Profile = -> Sketch018
  ReferenceAxis = -> Sketch018 [N_Axis]
  Refine = true
  Suppressed = false
  Type = 0
FEATURE [Sketcher::SketchObject] Sketch020
  ArcFitTolerance = 1e-06
  AttachmentSupport = -> [Pad012]
  ExternalGeometry = -> [Pad012]
  FullyConstrained = true
  MakeInternals = false
  MapMode = 5
  Placement = pos=(0,8.5e-14,386.284) rot=(0,0,1;0rad)
  sketch-geometry (4):
    g0: LineSegment StartX=-96.6131 StartY=-284 StartZ=0 EndX=96.814 EndY=-284 EndZ=0
    g1: LineSegment StartX=96.814 StartY=-284 StartZ=0 EndX=96.814 EndY=-249 EndZ=0
    g2: LineSegment StartX=96.814 StartY=-249 StartZ=0 EndX=-96.6131 EndY=-249 EndZ=0
    g3: LineSegment StartX=-96.6131 StartY=-249 StartZ=0 EndX=-96.6131 EndY=-284 EndZ=0
  constraints (12):
    c: Coincident(g0,g1)
    c: Coincident(g1,g2)
    c: Coincident(g2,g3)
    c: Coincident(g3,g0)
    c: Horizontal(g0)
    c: Horizontal(g2)
    c: Vertical(g1)
    c: Vertical(g3)
    c: PointOnObject(g2,g-7)
    c: DistanceX(g-5,g0) = 15
    c: DistanceX(g0,g-6) = 15
    c: DistanceY(g-6,g0) = 15
FEATURE [PartDesign::Pocket] Pocket007
  BaseFeature = -> Pad012
  Direction = (0,0,-1)
  Length = 5
  Length2 = 5
  Profile = -> Sketch020
  ReferenceAxis = -> Sketch020 [N_Axis]
  Refine = true
  Suppressed = false
  Type = 1
FEATURE [PartDesign::Fillet] Fillet012
  Base = -> Pocket007 [Edge18]
  BaseFeature = -> Pocket007
  Radius = 5
  Refine = true
  SupportTransform = false
  Suppressed = false
  UseAllEdges = false
FEATURE [PartDesign::Fillet] Fillet013
  Base = -> Fillet012 [Edge22,Edge35,Edge21,Edge36,Edge19,Edge37]
  BaseFeature = -> Fillet012
  Radius = 5
  Refine = true
  SupportTransform = false
  Suppressed = false
  UseAllEdges = false
FEATURE [PartDesign::Body] Body004
  AllowCompound = false
  Group = -> [CopyPocket014,Sketch018,Pad012,Sketch020,Pocket007,Fillet012,Fillet013]
  Origin = -> Origin004
  Tip = -> Fillet013
FEATURE [PartDesign::ShapeBinder] CopyPocket015
  TraceSupport = false
FEATURE [Sketcher::SketchObject] Sketch021
  ArcFitTolerance = 1e-06
  AttachmentSupport = -> [CopyPocket015]
  ExternalGeometry = -> [CopyPocket015]
  FullyConstrained = false
  MakeInternals = false
  MapMode = 5
  Placement = pos=(0,-249,0) rot=(1,0,0;1.5708rad)
  sketch-geometry (14):
    g0: LineSegment [constr] StartX=-160 StartY=332.961 StartZ=0 EndX=-175 EndY=332.942 EndZ=0
    g1: LineSegment [constr] StartX=-175 StartY=317.961 StartZ=0 EndX=-175 EndY=332.942 EndZ=0
    g2: LineSegment [constr] StartX=175 StartY=220.039 StartZ=0 EndX=175 EndY=205.039 EndZ=0
    g3: LineSegment [constr] StartX=160 StartY=205.039 StartZ=0 EndX=175 EndY=205.039 EndZ=0
    g4: LineSegment [constr] StartX=-214.5 StartY=414 StartZ=0 EndX=-254.5 EndY=414 EndZ=0
    g5: LineSegment [constr] StartX=-254.5 StartY=374 StartZ=0 EndX=-254.5 EndY=414 EndZ=0
    g6: LineSegment StartX=-254.5 StartY=374 StartZ=0 EndX=-254.5 EndY=124 EndZ=0
    g7: LineSegment StartX=-254.5 StartY=124 StartZ=0 EndX=254.5 EndY=124 EndZ=0
    g8: LineSegment StartX=254.5 StartY=124 StartZ=0 EndX=254.5 EndY=374 EndZ=0
    g9: LineSegment StartX=214.5 StartY=414 StartZ=0 EndX=-214.5 EndY=414 EndZ=0
    g10: ArcOfCircle CenterX=-214.5 CenterY=374 CenterZ=0 NormalX=0 NormalY=0 NormalZ=1 AngleXU=0 Radius=40 StartAngle=1.5708 EndAngle=3.14159
    g11: ArcOfCircle CenterX=214.5 CenterY=374 CenterZ=0 NormalX=0 NormalY=0 NormalZ=1 AngleXU=0 Radius=40 StartAngle=0 EndAngle=1.5708
    g12: GeomPoint [constr] X=-254.5 Y=414 Z=0
    g13: GeomPoint [constr] X=254.5 Y=124 Z=0
  constraints (27):
    c: Coincident(g1,g-7)
    c: Vertical(g1)
    c: PointOnObject(g0,g1)
    c: Coincident(g2,g-8)
    c: Vertical(g2)
    c: Coincident(g3,g-8)
    c: Horizontal(g3)
    c: Coincident(g2,g3)
    c: Coincident(g4,g-4)
    c: Horizontal(g4)
    c: Coincident(g5,g-3)
    c: Vertical(g5)
    c: Coincident(g4,g5)
    c: Tangent(g6,g10) = -1.5708
    c: Tangent(g8,g11) = -1.5708
    c: Tangent(g9,g11) = -1.5708
    c: Tangent(g9,g10) = -1.5708
    c: Vertical(g6)
    c: Vertical(g8)
    c: Horizontal(g9)
    c: PointOnObject(g12,g9)
    c: Coincident(g12,g4)
    c: Coincident(g13,g-6)
    c: Coincident(g8,g13)
    c: Coincident(g7,g8)
    c: Coincident(g7,g-5)
    c: Coincident(g6,g7)
FEATURE [PartDesign::Pad] Pad013
  Direction = (0,-1,2e-16)
  Length = 15
  Length2 = 10
  Profile = -> Sketch021
  ReferenceAxis = -> Sketch021 [N_Axis]
  Refine = true
  Reversed = true
  Suppressed = false
  Type = 0
FEATURE [Sketcher::SketchObject] Sketch022
  ArcFitTolerance = 1e-06
  AttachmentSupport = -> [Pad013]
  ExternalGeometry = -> [CopyPocket015]
  FullyConstrained = false
  MakeInternals = false
  MapMode = 5
  Placement = pos=(0,-249,0) rot=(1,0,0;1.5708rad)
  sketch-geometry (14):
    g0: LineSegment [constr] StartX=-160 StartY=332.961 StartZ=0 EndX=-175 EndY=332.942 EndZ=0
    g1: LineSegment [constr] StartX=-175 StartY=317.961 StartZ=0 EndX=-175 EndY=332.942 EndZ=0
    g2: LineSegment [constr] StartX=175 StartY=220.039 StartZ=0 EndX=175 EndY=205.039 EndZ=0
    g3: LineSegment [constr] StartX=160 StartY=205.039 StartZ=0 EndX=175 EndY=205.039 EndZ=0
    g4: LineSegment StartX=-175 StartY=317.975 StartZ=0 EndX=-175 EndY=220.006 EndZ=0
    g5: LineSegment StartX=-160.033 StartY=205.039 StartZ=0 EndX=160.033 EndY=205.039 EndZ=0
    g6: LineSegment StartX=175 StartY=220.006 StartZ=0 EndX=175 EndY=317.975 EndZ=0
    g7: LineSegment StartX=160.033 StartY=332.942 StartZ=0 EndX=-160.033 EndY=332.942 EndZ=0
    g8: ArcOfCircle CenterX=-160.033 CenterY=317.975 CenterZ=0 NormalX=0 NormalY=0 NormalZ=1 AngleXU=0 Radius=14.9674 StartAngle=1.5708 EndAngle=3.14159
    g9: ArcOfCircle CenterX=-160.033 CenterY=220.006 CenterZ=0 NormalX=0 NormalY=0 NormalZ=1 AngleXU=0 Radius=14.9674 StartAngle=3.14159 EndAngle=4.71239
    g10: ArcOfCircle CenterX=160.033 CenterY=220.006 CenterZ=0 NormalX=0 NormalY=0 NormalZ=1 AngleXU=0 Radius=14.9674 StartAngle=4.71239 EndAngle=6.28319
    g11: ArcOfCircle CenterX=160.033 CenterY=317.975 CenterZ=0 NormalX=0 NormalY=0 NormalZ=1 AngleXU=0 Radius=14.9674 StartAngle=0 EndAngle=1.5708
    g12: GeomPoint [constr] X=-175 Y=332.942 Z=0
    g13: GeomPoint [constr] X=175 Y=205.039 Z=0
  constraints (26):
    c: Vertical(g1)
    c: PointOnObject(g0,g1)
    c: Vertical(g2)
    c: Horizontal(g3)
    c: Coincident(g2,g3)
    c: Tangent(g4,g8) = -1.5708
    c: Tangent(g4,g9) = -1.5708
    c: Tangent(g5,g9) = -1.5708
    c: Tangent(g5,g10) = -1.5708
    c: Tangent(g6,g10) = -1.5708
    c: Tangent(g6,g11) = -1.5708
    c: Tangent(g7,g11) = -1.5708
    c: Tangent(g7,g8) = -1.5708
    c: Vertical(g4)
    c: Vertical(g6)
    c: Horizontal(g5)
    c: Horizontal(g7)
    c: Equal(g8,g9)
    c: Equal(g9,g10)
    c: Equal(g10,g11)
    c: PointOnObject(g12,g4)
    c: PointOnObject(g12,g7)
    c: PointOnObject(g13,g5)
    c: PointOnObject(g13,g6)
    c: Coincident(g12,g0)
    c: Coincident(g13,g2)
FEATURE [PartDesign::Pocket] Pocket008
  BaseFeature = -> Pad013
  Direction = (0,1,-2e-16)
  Length = 15
  Length2 = 5
  Profile = -> Sketch022
  ReferenceAxis = -> Sketch022 [N_Axis]
  Refine = true
  Suppressed = false
  Type = 0
FEATURE [PartDesign::Body] Body005
  AllowCompound = false
  Group = -> [CopyPocket015,Sketch021,Pad013,Sketch022,Pocket008]
  Origin = -> Origin005
  Tip = -> Pocket008
FEATURE [Sketcher::SketchObject] Sketch023
  ArcFitTolerance = 1e-06
  AttachmentSupport = -> [Pocket006]
  ExternalGeometry = -> [Pocket006]
  FullyConstrained = true
  MakeInternals = false
  MapMode = 5
  Placement = pos=(0,2.73e-14,124) rot=(1,0,0;3.14159rad)
  sketch-geometry (4):
    g0: LineSegment StartX=-254.5 StartY=249 StartZ=0 EndX=-254.5 EndY=234 EndZ=0
    g1: LineSegment StartX=-254.5 StartY=234 StartZ=0 EndX=254.5 EndY=234 EndZ=0
    g2: LineSegment StartX=254.5 StartY=234 StartZ=0 EndX=254.5 EndY=249 EndZ=0
    g3: LineSegment StartX=254.5 StartY=249 StartZ=0 EndX=-254.5 EndY=249 EndZ=0
  constraints (10):
    c: Coincident(g0,g1)
    c: Coincident(g1,g2)
    c: Coincident(g2,g3)
    c: Coincident(g3,g0)
    c: Vertical(g0)
    c: Vertical(g2)
    c: Horizontal(g1)
    c: Horizontal(g3)
    c: Coincident(g0,g-3)
    c: Coincident(g1,g-4)
FEATURE [PartDesign::Pocket] Pocket009
  BaseFeature = -> Pocket006
  Direction = (0,0,1)
  Length = 0
  Length2 = 5
  Profile = -> Sketch023
  ReferenceAxis = -> Sketch023 [N_Axis]
  Refine = true
  Suppressed = false
  Type = 3
  UpToFace = -> Pocket006 [Face5]
FEATURE [PartDesign::Body] Body
  AllowCompound = false
  Group = -> [Sketch,Pad,Sketch001,Pad001,Sketch002,Pad002,Sketch003,Pad003,Sketch004,Pad004,Sketch005,Pocket,Sketch006,Pocket001,Sketch007,Pad005,Sketch008,Pad006,Sketch009,Pocket002,Fillet,Fillet001,Fillet002,Fillet003,Fillet004,Fillet005,Fillet006,Fillet007,Sketch010,Pocket003,Sketch015,Pocket004,Sketch016,Pocket005,Sketch019,Pocket006,Sketch023,Pocket009]
  Origin = -> Origin
  Tip = -> Pocket009
FEATURE [Part::FeaturePython] Clone  label="body_clone"  # Draft clone (typed FeaturePython)
  AttacherType = Attacher::AttachEngine3D
  Fuse = false
  Objects = -> [Body]
  Scale = (1,1,1)
FEATURE [Part::FeaturePython] Clone001  label="left_switch_clone"  # Draft clone (typed FeaturePython)
  AttacherType = Attacher::AttachEngine3D
  Fuse = false
  Objects = -> [Body001]
  Scale = (1,1,1)
FEATURE [Part::FeaturePython] Clone002  label="right_switch_clone"  # Draft clone (typed FeaturePython)
  AttacherType = Attacher::AttachEngine3D
  Fuse = false
  Objects = -> [Body002]
  Scale = (1,1,1)
FEATURE [Part::FeaturePython] Clone003  label="handle_clone"  # Draft clone (typed FeaturePython)
  AttacherType = Attacher::AttachEngine3D
  Fuse = false
  Objects = -> [Body004]
  Scale = (1,1,1)
FEATURE [Part::FeaturePython] Clone004  label="fromt_panel_clone"  # Draft clone (typed FeaturePython)
  AttacherType = Attacher::AttachEngine3D
  Fuse = false
  Objects = -> [Body005]
  Scale = (1,1,1)
FEATURE [Part::FeaturePython] Clone005  label="glass_clone"  # Draft clone (typed FeaturePython)
  AttacherType = Attacher::AttachEngine3D
  Fuse = false
  Objects = -> [Body003]
  Scale = (1,1,1)
FEATURE [App::Part] Part  label="toasteroven"
  Group = -> [Clone,Clone001,Clone002,Clone003,Clone004,Clone005]
  Origin = -> Origin006
